# Revit family: W Shapes
name_source: partatom
category: Structural Framing
units: mm (PartAtom-declared; Revit-internal decimal feet)

## family parameters
Always export as geometry = No
Always vertical = Yes
Code Name = AISC 14.1
Cut with Voids When Loaded = No
Material for Model Behavior = Steel
OmniClass Number = 23.25.30.11.14.14
OmniClass Title = Beams
Section Shape = I-shape Parallel Flange
Shared = No
Show family pre-cut in plan views = Yes
Structural Framing Length Roundoff = 0' - 0"

## types (280) — shared parameters
Assembly Code = B10
Principal Axes Angle = 0.00°

## per-type parameters (varying)
| type | Bolt Spacing | Centroid Horizontal | Centroid Vertical | Elastic Modulus strong axis | Elastic Modulus weak axis | Flange Thickness | Height | Moment of Inertia strong axis | Moment of Inertia weak axis | Nominal Weight | Perimeter | Plastic Modulus strong axis | Plastic Modulus weak axis | Section Area | Section Name Key | Torsional Moment of Inertia | Warping Constant | Web Fillet | Web Thickness | Width |
| W12X26 | 0' - 3 1/2" | 3.245" | 6.100" | 33.40 in³ | 5.34 in³ | 0.380" | 12.200" | 204.0000 in⁴ | 17.3000 in⁴ | 26.00 lbf/ft | 49.40 ft²/ft | 37.20 in³ | 8.17 in³ | 7.65 in² | W12x26 | 0.3000 in⁴ | 607.00 in⁶ | 0.300" | 0.230" | 6.490" |
| W18X40 | 0' - 3 1/2" | 3.010" | 8.950" | 68.40 in³ | 6.35 in³ | 0.525" | 17.900" | 612.0000 in⁴ | 19.1000 in⁴ | 40.00 lbf/ft | 58.60 ft²/ft | 78.40 in³ | 10.00 in³ | 11.80 in² | W18x40 | 0.8100 in⁴ | 1440.00 in⁶ | 0.402" | 0.315" | 6.020" |
| W14x808 | 0' - 7 1/2" | 9.250" | 11.400" | 1400.00 in³ | 596.00 in³ | 5.120" | 22.800" | 16000.0000 in⁴ | 5550.0000 in⁴ | 808.00 lbf/ft | 111.34 ft²/ft | 1840.00 in³ | 930.00 in³ | 238.00 in² | W14x808 | 1840.0000 in⁴ | 435000.00 in⁶ | 0.600" | 3.740" | 18.500" |
| W14x873 | 0' - 7 1/2" | 9.350" | 11.800" | 1540.00 in³ | 655.00 in³ | 5.510" | 23.600" | 18200.0000 in⁴ | 6170.0000 in⁴ | 873.00 lbf/ft | 113.00 ft²/ft | 2030.00 in³ | 1020.00 in³ | 257.00 in² | W14x873 | 2270.0000 in⁴ | 505000.00 in⁶ | 0.600" | 3.940" | 18.700" |
| W36x723 | 0' - 7 1/2" | 8.900" | 20.900" | 2740.00 in³ | 415.00 in³ | 3.900" | 41.800" | 57200.0000 in⁴ | 3700.0000 in⁴ | 723.00 lbf/ft | 148.98 ft²/ft | 3270.00 in³ | 658.00 in³ | 213.00 in² | W36x723 | 785.0000 in⁴ | 1329000.00 in⁶ | 0.950" | 2.170" | 17.800" |
| W36x802 | 0' - 7 1/2" | 9.000" | 21.300" | 3040.00 in³ | 467.00 in³ | 4.290" | 42.600" | 64700.0000 in⁴ | 4210.0000 in⁴ | 802.00 lbf/ft | 151.06 ft²/ft | 3650.00 in³ | 744.00 in³ | 236.00 in² | W36x802 | 1040.0000 in⁴ | 1544000.00 in⁶ | 0.950" | 2.380" | 18.000" |
| W36x853 | 0' - 7 1/2" | 9.100" | 21.550" | 3240.00 in³ | 504.00 in³ | 4.530" | 43.100" | 69800.0000 in⁴ | 4600.0000 in⁴ | 853.00 lbf/ft | 152.36 ft²/ft | 3910.00 in³ | 805.00 in³ | 251.00 in² | W36x853 | 1240.0000 in⁴ | 1705000.00 in⁶ | 0.950" | 2.520" | 18.200" |
| W36x925 | 0' - 7 1/2" | 9.300" | 21.550" | 3380.00 in³ | 530.00 in³ | 4.530" | 43.100" | 72800.0000 in⁴ | 4940.0000 in⁴ | 925.00 lbf/ft | 153.27 ft²/ft | 4130.00 in³ | 862.00 in³ | 272.00 in² | W36x925 | 1430.0000 in⁴ | 1831000.00 in⁶ | 0.950" | 3.020" | 18.600" |
| W40x655 | 0' - 7 1/2" | 8.450" | 21.800" | 2600.00 in³ | 339.00 in³ | 3.540" | 43.600" | 56600.0000 in⁴ | 2870.0000 in⁴ | 655.00 lbf/ft | 148.66 ft²/ft | 3080.00 in³ | 542.00 in³ | 193.00 in² | W40x655 | 589.0000 in⁴ | 1154000.00 in⁶ | 0.790" | 1.970" | 16.900" |
| W4X13 | 0' - 2 1/4" | 2.030" | 2.080" | 5.46 in³ | 1.90 in³ | 0.345" | 4.160" | 11.3000 in⁴ | 3.8600 in⁴ | 13.00 lbf/ft | 23.60 ft²/ft | 6.28 in³ | 2.92 in³ | 3.83 in² | W4x13 | 0.1510 in⁴ | 14.00 in⁶ | 0.250" | 0.280" | 4.060" |
| W5X16 | 0' - 2 3/4" | 2.500" | 2.505" | 8.55 in³ | 3.00 in³ | 0.360" | 5.010" | 21.4000 in⁴ | 7.5100 in⁴ | 16.00 lbf/ft | 29.00 ft²/ft | 9.63 in³ | 4.58 in³ | 4.71 in² | W5x16 | 0.1920 in⁴ | 40.60 in⁶ | 0.300" | 0.240" | 5.000" |
| W5X19 | 0' - 2 3/4" | 2.515" | 2.575" | 10.20 in³ | 3.63 in³ | 0.430" | 5.150" | 26.3000 in⁴ | 9.1300 in⁴ | 19.00 lbf/ft | 29.40 ft²/ft | 11.60 in³ | 5.53 in³ | 5.56 in² | W5x19 | 0.3160 in⁴ | 50.90 in⁶ | 0.300" | 0.270" | 5.030" |
| W6X8.5 | 0' - 2 1/4" | 1.970" | 2.915" | 5.10 in³ | 1.01 in³ | 0.195" | 5.830" | 14.9000 in⁴ | 1.9900 in⁴ | 8.50 lbf/ft | 26.70 ft²/ft | 5.73 in³ | 1.56 in³ | 2.52 in² | W6x8.5 | 0.0333 in⁴ | 15.80 in⁶ | 0.250" | 0.170" | 3.940" |
| W6X9 | 0' - 2 1/4" | 1.970" | 2.950" | 5.56 in³ | 1.11 in³ | 0.215" | 5.900" | 16.4000 in⁴ | 2.2000 in⁴ | 9.00 lbf/ft | 26.80 ft²/ft | 6.23 in³ | 1.72 in³ | 2.68 in² | W6x9 | 0.0405 in⁴ | 17.70 in⁶ | 0.250" | 0.170" | 3.940" |
| W6X12 | 0' - 2 1/4" | 2.000" | 3.015" | 7.31 in³ | 1.50 in³ | 0.280" | 6.030" | 22.1000 in⁴ | 2.9900 in⁴ | 12.00 lbf/ft | 27.20 ft²/ft | 8.30 in³ | 2.32 in³ | 3.55 in² | W6x12 | 0.0903 in⁴ | 24.70 in⁶ | 0.250" | 0.230" | 4.000" |
| W6X15 | 0' - 3 1/2" | 2.995" | 2.995" | 9.72 in³ | 3.11 in³ | 0.260" | 5.990" | 29.1000 in⁴ | 9.3200 in⁴ | 15.00 lbf/ft | 35.10 ft²/ft | 10.80 in³ | 4.75 in³ | 4.43 in² | W6x15 | 0.1010 in⁴ | 76.50 in⁶ | 0.250" | 0.230" | 5.990" |
| W6X16 | 0' - 2 1/4" | 2.015" | 3.140" | 10.20 in³ | 2.20 in³ | 0.405" | 6.280" | 32.1000 in⁴ | 4.4300 in⁴ | 16.00 lbf/ft | 27.70 ft²/ft | 11.70 in³ | 3.39 in³ | 4.74 in² | W6x16 | 0.2230 in⁴ | 38.20 in⁶ | 0.250" | 0.260" | 4.030" |
| W6X20 | 0' - 3 1/2" | 3.010" | 3.100" | 13.40 in³ | 4.41 in³ | 0.365" | 6.200" | 41.4000 in⁴ | 13.3000 in⁴ | 20.00 lbf/ft | 35.50 ft²/ft | 15.00 in³ | 6.72 in³ | 5.87 in² | W6x20 | 0.2400 in⁴ | 113.00 in⁶ | 0.250" | 0.260" | 6.020" |
| W6X25 | 0' - 3 1/2" | 3.040" | 3.190" | 16.70 in³ | 5.61 in³ | 0.455" | 6.380" | 53.4000 in⁴ | 17.1000 in⁴ | 25.00 lbf/ft | 36.00 ft²/ft | 18.90 in³ | 8.56 in³ | 7.34 in² | W6x25 | 0.4610 in⁴ | 150.00 in⁶ | 0.250" | 0.320" | 6.080" |
| W8X10 | 0' - 2 1/4" | 1.970" | 3.945" | 7.81 in³ | 1.06 in³ | 0.205" | 7.890" | 30.8000 in⁴ | 2.0900 in⁴ | 10.00 lbf/ft | 30.70 ft²/ft | 8.87 in³ | 1.66 in³ | 2.96 in² | W8x10 | 0.0426 in⁴ | 30.90 in⁶ | 0.300" | 0.170" | 3.940" |
| W8X13 | 0' - 2 1/4" | 2.000" | 3.995" | 9.91 in³ | 1.37 in³ | 0.255" | 7.990" | 39.6000 in⁴ | 2.7300 in⁴ | 13.00 lbf/ft | 31.00 ft²/ft | 11.40 in³ | 2.15 in³ | 3.84 in² | W8x13 | 0.0871 in⁴ | 40.80 in⁶ | 0.300" | 0.230" | 4.000" |
| W8X15 | 0' - 2 1/4" | 2.008" | 4.055" | 11.80 in³ | 1.70 in³ | 0.315" | 8.110" | 48.0000 in⁴ | 3.4100 in⁴ | 15.00 lbf/ft | 31.30 ft²/ft | 13.60 in³ | 2.67 in³ | 4.44 in² | W8x15 | 0.1370 in⁴ | 51.80 in⁶ | 0.300" | 0.245" | 4.015" |
| W8X18 | 0' - 2 3/4" | 2.625" | 4.070" | 15.20 in³ | 3.04 in³ | 0.330" | 8.140" | 61.9000 in⁴ | 7.9700 in⁴ | 18.00 lbf/ft | 36.30 ft²/ft | 17.00 in³ | 4.66 in³ | 5.26 in² | W8x18 | 0.1720 in⁴ | 122.00 in⁶ | 0.300" | 0.230" | 5.250" |
| W8X21 | 0' - 2 3/4" | 2.635" | 4.140" | 18.20 in³ | 3.71 in³ | 0.400" | 8.280" | 75.3000 in⁴ | 9.7700 in⁴ | 21.00 lbf/ft | 36.60 ft²/ft | 20.40 in³ | 5.69 in³ | 6.16 in² | W8x21 | 0.2820 in⁴ | 152.00 in⁶ | 0.300" | 0.250" | 5.270" |
| W8X24 | 0' - 4" | 3.250" | 3.965" | 20.90 in³ | 5.63 in³ | 0.400" | 7.930" | 82.7000 in⁴ | 18.3000 in⁴ | 24.00 lbf/ft | 40.70 ft²/ft | 23.10 in³ | 8.57 in³ | 7.08 in² | W8x24 | 0.3460 in⁴ | 259.00 in⁶ | 0.394" | 0.245" | 6.500" |
| W8X28 | 0' - 4" | 3.270" | 4.030" | 24.30 in³ | 6.63 in³ | 0.465" | 8.060" | 98.0000 in⁴ | 21.7000 in⁴ | 28.00 lbf/ft | 41.00 ft²/ft | 27.20 in³ | 10.10 in³ | 8.25 in² | W8x28 | 0.5370 in⁴ | 312.00 in⁶ | 0.394" | 0.285" | 6.540" |
| W8X31 | 0' - 5 1/2" | 4.000" | 4.000" | 27.50 in³ | 9.27 in³ | 0.435" | 8.000" | 110.0000 in⁴ | 37.1000 in⁴ | 31.00 lbf/ft | 46.80 ft²/ft | 30.40 in³ | 14.10 in³ | 9.13 in² | W8x31 | 0.5360 in⁴ | 530.00 in⁶ | 0.394" | 0.285" | 8.000" |
| W8X35 | 0' - 5 1/2" | 4.010" | 4.060" | 31.20 in³ | 10.60 in³ | 0.495" | 8.120" | 127.0000 in⁴ | 42.6000 in⁴ | 35.00 lbf/ft | 47.00 ft²/ft | 34.70 in³ | 16.10 in³ | 10.30 in² | W8x35 | 0.7690 in⁴ | 619.00 in⁶ | 0.394" | 0.310" | 8.020" |
| W8X40 | 0' - 5 1/2" | 4.035" | 4.125" | 35.50 in³ | 12.20 in³ | 0.560" | 8.250" | 146.0000 in⁴ | 49.1000 in⁴ | 40.00 lbf/ft | 47.40 ft²/ft | 39.80 in³ | 18.50 in³ | 11.70 in² | W8x40 | 1.1200 in⁴ | 726.00 in⁶ | 0.394" | 0.360" | 8.070" |
| W8X48 | 0' - 5 1/2" | 4.055" | 4.250" | 43.20 in³ | 15.00 in³ | 0.685" | 8.500" | 184.0000 in⁴ | 60.9000 in⁴ | 48.00 lbf/ft | 48.00 ft²/ft | 49.00 in³ | 22.90 in³ | 14.10 in² | W8x48 | 1.9600 in⁴ | 931.00 in⁶ | 0.395" | 0.400" | 8.110" |
| W8X58 | 0' - 5 1/2" | 4.110" | 4.375" | 52.00 in³ | 18.30 in³ | 0.810" | 8.750" | 228.0000 in⁴ | 75.1000 in⁴ | 58.00 lbf/ft | 48.70 ft²/ft | 59.80 in³ | 27.90 in³ | 17.10 in² | W8x58 | 3.3300 in⁴ | 1180.00 in⁶ | 0.390" | 0.510" | 8.220" |
| W8X67 | 0' - 5 1/2" | 4.140" | 4.500" | 60.40 in³ | 21.40 in³ | 0.935" | 9.000" | 272.0000 in⁴ | 88.6000 in⁴ | 67.00 lbf/ft | 49.30 ft²/ft | 70.10 in³ | 32.70 in³ | 19.70 in² | W8x67 | 5.0500 in⁴ | 1440.00 in⁶ | 0.395" | 0.570" | 8.280" |
| W10X12 | 0' - 2 1/4" | 1.980" | 4.935" | 10.90 in³ | 1.10 in³ | 0.210" | 9.870" | 53.8000 in⁴ | 2.1800 in⁴ | 12.00 lbf/ft | 34.70 ft²/ft | 12.60 in³ | 1.74 in³ | 3.54 in² | W10x12 | 0.0547 in⁴ | 50.90 in⁶ | 0.300" | 0.190" | 3.960" |
| W10X15 | 0' - 2 1/4" | 2.000" | 4.995" | 13.80 in³ | 1.45 in³ | 0.270" | 9.990" | 68.9000 in⁴ | 2.8900 in⁴ | 15.00 lbf/ft | 35.00 ft²/ft | 16.00 in³ | 2.30 in³ | 4.41 in² | W10x15 | 0.1040 in⁴ | 68.30 in⁶ | 0.300" | 0.230" | 4.000" |
| W10X17 | 0' - 2 1/4" | 2.005" | 5.050" | 16.20 in³ | 1.78 in³ | 0.330" | 10.100" | 81.9000 in⁴ | 3.5600 in⁴ | 17.00 lbf/ft | 35.20 ft²/ft | 18.70 in³ | 2.80 in³ | 4.99 in² | W10x17 | 0.1560 in⁴ | 85.10 in⁶ | 0.300" | 0.240" | 4.010" |
| W10X19 | 0' - 2 1/4" | 2.010" | 5.100" | 18.80 in³ | 2.14 in³ | 0.395" | 10.200" | 96.3000 in⁴ | 4.2900 in⁴ | 19.00 lbf/ft | 35.50 ft²/ft | 21.60 in³ | 3.35 in³ | 5.62 in² | W10x19 | 0.2330 in⁴ | 104.00 in⁶ | 0.300" | 0.250" | 4.020" |
| W10X22 | 0' - 2 3/4" | 2.875" | 5.100" | 23.20 in³ | 3.97 in³ | 0.360" | 10.200" | 118.0000 in⁴ | 11.4000 in⁴ | 22.00 lbf/ft | 42.40 ft²/ft | 26.00 in³ | 6.10 in³ | 6.49 in² | W10x22 | 0.2390 in⁴ | 275.00 in⁶ | 0.300" | 0.240" | 5.750" |
| W10X26 | 0' - 2 3/4" | 2.885" | 5.150" | 27.90 in³ | 4.89 in³ | 0.440" | 10.300" | 144.0000 in⁴ | 14.1000 in⁴ | 26.00 lbf/ft | 42.60 ft²/ft | 31.30 in³ | 7.50 in³ | 7.61 in² | W10x26 | 0.4020 in⁴ | 345.00 in⁶ | 0.300" | 0.260" | 5.770" |
| W10X30 | 0' - 2 3/4" | 2.905" | 5.250" | 32.40 in³ | 5.75 in³ | 0.510" | 10.500" | 170.0000 in⁴ | 16.7000 in⁴ | 30.00 lbf/ft | 43.10 ft²/ft | 36.60 in³ | 8.84 in³ | 8.84 in² | W10x30 | 0.6220 in⁴ | 414.00 in⁶ | 0.300" | 0.300" | 5.810" |
| W10X33 | 0' - 5 1/2" | 3.980" | 4.865" | 35.00 in³ | 9.20 in³ | 0.435" | 9.730" | 171.0000 in⁴ | 36.6000 in⁴ | 33.00 lbf/ft | 49.90 ft²/ft | 38.80 in³ | 14.00 in³ | 9.71 in² | W10x33 | 0.5830 in⁴ | 791.00 in⁶ | 0.500" | 0.290" | 7.960" |
| W10X39 | 0' - 5 1/2" | 3.995" | 4.960" | 42.10 in³ | 11.30 in³ | 0.530" | 9.920" | 209.0000 in⁴ | 45.0000 in⁴ | 39.00 lbf/ft | 50.30 ft²/ft | 46.80 in³ | 17.20 in³ | 11.50 in² | W10x39 | 0.9760 in⁴ | 992.00 in⁶ | 0.500" | 0.315" | 7.990" |
| W10X45 | 0' - 5 1/2" | 4.010" | 5.050" | 49.10 in³ | 13.30 in³ | 0.620" | 10.100" | 248.0000 in⁴ | 53.4000 in⁴ | 45.00 lbf/ft | 50.70 ft²/ft | 54.90 in³ | 20.30 in³ | 13.30 in² | W10x45 | 1.5100 in⁴ | 1200.00 in⁶ | 0.500" | 0.350" | 8.020" |
| W10X49 | 0' - 5 1/2" | 5.000" | 5.000" | 54.60 in³ | 18.70 in³ | 0.560" | 10.000" | 272.0000 in⁴ | 93.4000 in⁴ | 49.00 lbf/ft | 58.50 ft²/ft | 60.40 in³ | 28.30 in³ | 14.40 in² | W10x49 | 1.3900 in⁴ | 2070.00 in⁶ | 0.500" | 0.340" | 10.000" |
| W10X54 | 0' - 5 1/2" | 5.000" | 5.050" | 60.00 in³ | 20.60 in³ | 0.615" | 10.100" | 303.0000 in⁴ | 103.0000 in⁴ | 54.00 lbf/ft | 58.60 ft²/ft | 66.60 in³ | 31.30 in³ | 15.80 in² | W10x54 | 1.8200 in⁴ | 2320.00 in⁶ | 0.505" | 0.370" | 10.000" |
| W10X60 | 0' - 5 1/2" | 5.050" | 5.100" | 66.70 in³ | 23.00 in³ | 0.680" | 10.200" | 341.0000 in⁴ | 116.0000 in⁴ | 60.00 lbf/ft | 59.10 ft²/ft | 74.60 in³ | 35.00 in³ | 17.70 in² | W10x60 | 2.4800 in⁴ | 2640.00 in⁶ | 0.500" | 0.420" | 10.100" |
| W10X68 | 0' - 5 1/2" | 5.050" | 5.200" | 75.70 in³ | 26.40 in³ | 0.770" | 10.400" | 394.0000 in⁴ | 134.0000 in⁴ | 68.00 lbf/ft | 59.40 ft²/ft | 85.30 in³ | 40.10 in³ | 19.90 in² | W10x68 | 3.5600 in⁴ | 3100.00 in⁶ | 0.500" | 0.470" | 10.100" |
| W10X77 | 0' - 5 1/2" | 5.100" | 5.300" | 85.90 in³ | 30.10 in³ | 0.870" | 10.600" | 455.0000 in⁴ | 154.0000 in⁴ | 77.00 lbf/ft | 60.10 ft²/ft | 97.60 in³ | 45.90 in³ | 22.70 in² | W10x77 | 5.1100 in⁴ | 3630.00 in⁶ | 0.500" | 0.530" | 10.200" |
| W10X88 | 0' - 5 1/2" | 5.150" | 5.400" | 98.50 in³ | 34.80 in³ | 0.990" | 10.800" | 534.0000 in⁴ | 179.0000 in⁴ | 88.00 lbf/ft | 60.70 ft²/ft | 113.00 in³ | 53.10 in³ | 26.00 in² | W10x88 | 7.5300 in⁴ | 4330.00 in⁶ | 0.500" | 0.605" | 10.300" |
| W10X100 | 0' - 5 1/2" | 5.150" | 5.550" | 112.00 in³ | 40.00 in³ | 1.120" | 11.100" | 623.0000 in⁴ | 207.0000 in⁴ | 100.00 lbf/ft | 61.20 ft²/ft | 130.00 in³ | 61.00 in³ | 29.30 in² | W10x100 | 10.9000 in⁴ | 5150.00 in⁶ | 0.500" | 0.680" | 10.300" |
| W10X112 | 0' - 5 1/2" | 5.200" | 5.700" | 126.00 in³ | 45.30 in³ | 1.250" | 11.400" | 716.0000 in⁴ | 236.0000 in⁴ | 112.00 lbf/ft | 62.00 ft²/ft | 147.00 in³ | 69.20 in³ | 32.90 in² | W10x112 | 15.1000 in⁴ | 6020.00 in⁶ | 0.500" | 0.755" | 10.400" |
| W12X14 | 0' - 2 1/4" | 1.985" | 5.950" | 14.90 in³ | 1.19 in³ | 0.225" | 11.900" | 88.6000 in⁴ | 2.3600 in⁴ | 14.00 lbf/ft | 38.80 ft²/ft | 17.40 in³ | 1.90 in³ | 4.16 in² | W12x14 | 0.0704 in⁴ | 80.40 in⁶ | 0.300" | 0.200" | 3.970" |
| W12X16 | 0' - 2 1/4" | 1.995" | 6.000" | 17.10 in³ | 1.41 in³ | 0.265" | 12.000" | 103.0000 in⁴ | 2.8200 in⁴ | 16.00 lbf/ft | 39.00 ft²/ft | 20.10 in³ | 2.26 in³ | 4.71 in² | W12x16 | 0.1030 in⁴ | 96.90 in⁶ | 0.300" | 0.220" | 3.990" |
| W12X19 | 0' - 2 1/4" | 2.005" | 6.100" | 21.30 in³ | 1.88 in³ | 0.350" | 12.200" | 130.0000 in⁴ | 3.7600 in⁴ | 19.00 lbf/ft | 39.50 ft²/ft | 24.70 in³ | 2.98 in³ | 5.57 in² | W12x19 | 0.1800 in⁴ | 131.00 in⁶ | 0.300" | 0.235" | 4.010" |
| W12X22 | 0' - 2 1/4" | 2.015" | 6.150" | 25.40 in³ | 2.31 in³ | 0.425" | 12.300" | 156.0000 in⁴ | 4.6600 in⁴ | 22.00 lbf/ft | 39.70 ft²/ft | 29.30 in³ | 3.66 in³ | 6.48 in² | W12x22 | 0.2930 in⁴ | 164.00 in⁶ | 0.300" | 0.260" | 4.030" |
| W12X30 | 0' - 3 1/2" | 3.260" | 6.150" | 38.60 in³ | 6.24 in³ | 0.440" | 12.300" | 238.0000 in⁴ | 20.3000 in⁴ | 30.00 lbf/ft | 49.60 ft²/ft | 43.10 in³ | 9.56 in³ | 8.79 in² | W12x30 | 0.4570 in⁴ | 720.00 in⁶ | 0.300" | 0.260" | 6.520" |
| W12X35 | 0' - 3 1/2" | 3.280" | 6.250" | 45.60 in³ | 7.47 in³ | 0.520" | 12.500" | 285.0000 in⁴ | 24.5000 in⁴ | 35.00 lbf/ft | 50.10 ft²/ft | 51.20 in³ | 11.50 in³ | 10.30 in² | W12x35 | 0.7410 in⁴ | 879.00 in⁶ | 0.300" | 0.300" | 6.560" |
| W12X40 | 0' - 5 1/2" | 4.005" | 5.950" | 51.50 in³ | 11.00 in³ | 0.515" | 11.900" | 307.0000 in⁴ | 44.1000 in⁴ | 40.00 lbf/ft | 54.40 ft²/ft | 57.00 in³ | 16.80 in³ | 11.70 in² | W12x40 | 0.9060 in⁴ | 1440.00 in⁶ | 0.505" | 0.295" | 8.010" |
| W12X45 | 0' - 5 1/2" | 4.025" | 6.050" | 57.70 in³ | 12.40 in³ | 0.575" | 12.100" | 348.0000 in⁴ | 50.0000 in⁴ | 45.00 lbf/ft | 54.90 ft²/ft | 64.20 in³ | 19.00 in³ | 13.10 in² | W12x45 | 1.2600 in⁴ | 1650.00 in⁶ | 0.505" | 0.335" | 8.050" |
| W12X50 | 0' - 5 1/2" | 4.040" | 6.100" | 64.20 in³ | 13.90 in³ | 0.640" | 12.200" | 391.0000 in⁴ | 56.3000 in⁴ | 50.00 lbf/ft | 55.10 ft²/ft | 71.90 in³ | 21.30 in³ | 14.60 in² | W12x50 | 1.7100 in⁴ | 1880.00 in⁶ | 0.500" | 0.370" | 8.080" |
| W12X53 | 0' - 5 1/2" | 5.000" | 6.050" | 70.60 in³ | 19.20 in³ | 0.575" | 12.100" | 425.0000 in⁴ | 95.8000 in⁴ | 53.00 lbf/ft | 62.50 ft²/ft | 77.90 in³ | 29.10 in³ | 15.60 in² | W12x53 | 1.5800 in⁴ | 3160.00 in⁶ | 0.605" | 0.345" | 10.000" |
| W12X58 | 0' - 5 1/2" | 5.000" | 6.100" | 78.00 in³ | 21.40 in³ | 0.640" | 12.200" | 475.0000 in⁴ | 107.0000 in⁴ | 58.00 lbf/ft | 62.60 ft²/ft | 86.40 in³ | 32.50 in³ | 17.00 in² | W12x58 | 2.1000 in⁴ | 3570.00 in⁶ | 0.600" | 0.360" | 10.000" |
| W12X65 | 0' - 5 1/2" | 6.000" | 6.050" | 87.90 in³ | 29.10 in³ | 0.605" | 12.100" | 533.0000 in⁴ | 174.0000 in⁴ | 65.00 lbf/ft | 70.40 ft²/ft | 96.80 in³ | 44.10 in³ | 19.10 in² | W12x65 | 2.1800 in⁴ | 5780.00 in⁶ | 0.595" | 0.390" | 12.000" |
| W12X72 | 0' - 5 1/2" | 6.000" | 6.150" | 97.40 in³ | 32.40 in³ | 0.670" | 12.300" | 597.0000 in⁴ | 195.0000 in⁴ | 72.00 lbf/ft | 70.70 ft²/ft | 108.00 in³ | 49.20 in³ | 21.10 in² | W12x72 | 2.9300 in⁴ | 6540.00 in⁶ | 0.600" | 0.430" | 12.000" |
| W12X79 | 0' - 5 1/2" | 6.050" | 6.200" | 107.00 in³ | 35.80 in³ | 0.735" | 12.400" | 662.0000 in⁴ | 216.0000 in⁴ | 79.00 lbf/ft | 71.20 ft²/ft | 119.00 in³ | 54.30 in³ | 23.20 in² | W12x79 | 3.8400 in⁴ | 7330.00 in⁶ | 0.595" | 0.470" | 12.100" |
| W12X87 | 0' - 5 1/2" | 6.050" | 6.250" | 118.00 in³ | 39.70 in³ | 0.810" | 12.500" | 740.0000 in⁴ | 241.0000 in⁴ | 87.00 lbf/ft | 71.30 ft²/ft | 132.00 in³ | 60.40 in³ | 25.60 in² | W12x87 | 5.1000 in⁴ | 8270.00 in⁶ | 0.600" | 0.515" | 12.100" |
| W12X96 | 0' - 5 1/2" | 6.100" | 6.350" | 131.00 in³ | 44.40 in³ | 0.900" | 12.700" | 833.0000 in⁴ | 270.0000 in⁴ | 96.00 lbf/ft | 72.10 ft²/ft | 147.00 in³ | 67.50 in³ | 28.20 in² | W12x96 | 6.8500 in⁴ | 9410.00 in⁶ | 0.600" | 0.550" | 12.200" |
| W12X106 | 0' - 5 1/2" | 6.100" | 6.450" | 145.00 in³ | 49.30 in³ | 0.990" | 12.900" | 933.0000 in⁴ | 301.0000 in⁴ | 106.00 lbf/ft | 72.40 ft²/ft | 164.00 in³ | 75.10 in³ | 31.20 in² | W12x106 | 9.1300 in⁴ | 10700.00 in⁶ | 0.600" | 0.610" | 12.200" |
| W12X120 | 0' - 5 1/2" | 6.150" | 6.550" | 163.00 in³ | 56.00 in³ | 1.110" | 13.100" | 1070.0000 in⁴ | 345.0000 in⁴ | 120.00 lbf/ft | 73.00 ft²/ft | 186.00 in³ | 85.40 in³ | 35.20 in² | W12x120 | 12.9000 in⁴ | 12400.00 in⁶ | 0.590" | 0.710" | 12.300" |
| W12X136 | 0' - 5 1/2" | 6.200" | 6.700" | 186.00 in³ | 64.20 in³ | 1.250" | 13.400" | 1240.0000 in⁴ | 398.0000 in⁴ | 136.00 lbf/ft | 73.80 ft²/ft | 214.00 in³ | 98.00 in³ | 39.90 in² | W12x136 | 18.5000 in⁴ | 14700.00 in⁶ | 0.600" | 0.790" | 12.400" |
| W12X152 | 0' - 5 1/2" | 6.250" | 6.850" | 209.00 in³ | 72.80 in³ | 1.400" | 13.700" | 1430.0000 in⁴ | 454.0000 in⁴ | 152.00 lbf/ft | 74.60 ft²/ft | 243.00 in³ | 111.00 in³ | 44.70 in² | W12x152 | 25.8000 in⁴ | 17200.00 in⁶ | 0.600" | 0.870" | 12.500" |
| W12X170 | 0' - 5 1/2" | 6.300" | 7.000" | 235.00 in³ | 82.30 in³ | 1.560" | 14.000" | 1650.0000 in⁴ | 517.0000 in⁴ | 170.00 lbf/ft | 75.50 ft²/ft | 275.00 in³ | 126.00 in³ | 50.00 in² | W12x170 | 35.6000 in⁴ | 20100.00 in⁶ | 0.600" | 0.960" | 12.600" |
| W12X190 | 0' - 5 1/2" | 6.350" | 7.200" | 263.00 in³ | 93.00 in³ | 1.740" | 14.400" | 1890.0000 in⁴ | 589.0000 in⁴ | 190.00 lbf/ft | 76.50 ft²/ft | 311.00 in³ | 143.00 in³ | 56.00 in² | W12x190 | 48.8000 in⁴ | 23600.00 in⁶ | 0.590" | 1.060" | 12.700" |
| W12X210 | 0' - 5 1/2" | 6.400" | 7.350" | 292.00 in³ | 104.00 in³ | 1.900" | 14.700" | 2140.0000 in⁴ | 664.0000 in⁴ | 210.00 lbf/ft | 77.20 ft²/ft | 348.00 in³ | 159.00 in³ | 61.80 in² | W12x210 | 64.7000 in⁴ | 27200.00 in⁶ | 0.600" | 1.180" | 12.800" |
| W12X230 | 0' - 5 1/2" | 6.450" | 7.550" | 321.00 in³ | 115.00 in³ | 2.070" | 15.100" | 2420.0000 in⁴ | 742.0000 in⁴ | 230.00 lbf/ft | 78.20 ft²/ft | 386.00 in³ | 177.00 in³ | 67.70 in² | W12x230 | 83.8000 in⁴ | 31200.00 in⁶ | 0.600" | 1.290" | 12.900" |
| W12X252 | 0' - 5 1/2" | 6.500" | 7.700" | 353.00 in³ | 127.00 in³ | 2.250" | 15.400" | 2720.0000 in⁴ | 828.0000 in⁴ | 252.00 lbf/ft | 79.00 ft²/ft | 428.00 in³ | 196.00 in³ | 74.10 in² | W12x252 | 108.0000 in⁴ | 35800.00 in⁶ | 0.600" | 1.400" | 13.000" |
| W12X279 | 0' - 5 1/2" | 6.550" | 7.950" | 393.00 in³ | 143.00 in³ | 2.470" | 15.900" | 3110.0000 in⁴ | 937.0000 in⁴ | 279.00 lbf/ft | 80.10 ft²/ft | 481.00 in³ | 220.00 in³ | 81.90 in² | W12x279 | 143.0000 in⁴ | 42000.00 in⁶ | 0.600" | 1.530" | 13.100" |
| W12X305 | 0' - 5 1/2" | 6.600" | 8.150" | 435.00 in³ | 159.00 in³ | 2.710" | 16.300" | 3550.0000 in⁴ | 1050.0000 in⁴ | 305.00 lbf/ft | 81.10 ft²/ft | 537.00 in³ | 244.00 in³ | 89.50 in² | W12x305 | 185.0000 in⁴ | 48600.00 in⁶ | 0.590" | 1.630" | 13.200" |
| W12X336 | 0' - 5 1/2" | 6.700" | 8.400" | 483.00 in³ | 177.00 in³ | 2.960" | 16.800" | 4060.0000 in⁴ | 1190.0000 in⁴ | 336.00 lbf/ft | 82.60 ft²/ft | 603.00 in³ | 274.00 in³ | 98.90 in² | W12x336 | 243.0000 in⁴ | 57000.00 in⁶ | 0.590" | 1.780" | 13.400" |
| W14X22 | 0' - 2 3/4" | 2.500" | 6.850" | 29.00 in³ | 2.80 in³ | 0.335" | 13.700" | 199.0000 in⁴ | 7.0000 in⁴ | 22.00 lbf/ft | 46.70 ft²/ft | 33.20 in³ | 4.39 in³ | 6.49 in² | W14x22 | 0.2080 in⁴ | 314.00 in⁶ | 0.400" | 0.230" | 5.000" |
| W14X26 | 0' - 3 1/2" | 2.515" | 6.950" | 35.30 in³ | 3.55 in³ | 0.420" | 13.900" | 245.0000 in⁴ | 8.9100 in⁴ | 26.00 lbf/ft | 53.30 ft²/ft | 40.20 in³ | 5.54 in³ | 7.69 in² | W14x26 | 0.3580 in⁴ | 405.00 in⁶ | 0.400" | 0.255" | 5.030" |
| W14X30 | 0' - 3 1/2" | 3.365" | 6.900" | 42.00 in³ | 5.82 in³ | 0.385" | 13.800" | 291.0000 in⁴ | 19.6000 in⁴ | 30.00 lbf/ft | 53.70 ft²/ft | 47.30 in³ | 8.99 in³ | 8.85 in² | W14x30 | 0.3800 in⁴ | 887.00 in⁶ | 0.400" | 0.270" | 6.730" |
| W14X34 | 0' - 7 1/2" | 3.375" | 7.000" | 48.60 in³ | 6.91 in³ | 0.455" | 14.000" | 340.0000 in⁴ | 23.3000 in⁴ | 34.00 lbf/ft | 97.50 ft²/ft | 54.60 in³ | 10.60 in³ | 10.00 in² | W14x34 | 0.5690 in⁴ | 1070.00 in⁶ | 0.400" | 0.285" | 6.750" |
| W14X38 | 0' - 3 1/2" | 3.385" | 7.050" | 54.60 in³ | 7.88 in³ | 0.515" | 14.100" | 385.0000 in⁴ | 26.7000 in⁴ | 38.00 lbf/ft | 54.00 ft²/ft | 61.50 in³ | 12.10 in³ | 11.20 in² | W14x38 | 0.7980 in⁴ | 1230.00 in⁶ | 0.400" | 0.310" | 6.770" |
| W14X43 | 0' - 5 1/2" | 4.000" | 6.850" | 62.60 in³ | 11.30 in³ | 0.530" | 13.700" | 428.0000 in⁴ | 45.2000 in⁴ | 43.00 lbf/ft | 57.80 ft²/ft | 69.60 in³ | 17.30 in³ | 12.60 in² | W14x43 | 1.0500 in⁴ | 1950.00 in⁶ | 0.590" | 0.305" | 8.000" |
| W14X48 | 0' - 5 1/2" | 4.015" | 6.900" | 70.20 in³ | 12.80 in³ | 0.595" | 13.800" | 484.0000 in⁴ | 51.4000 in⁴ | 48.00 lbf/ft | 58.00 ft²/ft | 78.40 in³ | 19.60 in³ | 14.10 in² | W14x48 | 1.4500 in⁴ | 2240.00 in⁶ | 0.595" | 0.340" | 8.030" |
| W14X53 | 0' - 5 1/2" | 4.030" | 6.950" | 77.80 in³ | 14.30 in³ | 0.660" | 13.900" | 541.0000 in⁴ | 57.7000 in⁴ | 53.00 lbf/ft | 58.30 ft²/ft | 87.10 in³ | 22.00 in³ | 15.60 in² | W14x53 | 1.9400 in⁴ | 2540.00 in⁶ | 0.590" | 0.370" | 8.060" |
| W14X61 | 0' - 5 1/2" | 5.000" | 6.950" | 92.10 in³ | 21.50 in³ | 0.645" | 13.900" | 640.0000 in⁴ | 107.0000 in⁴ | 61.00 lbf/ft | 66.00 ft²/ft | 102.00 in³ | 32.80 in³ | 17.90 in² | W14x61 | 2.1900 in⁴ | 4710.00 in⁶ | 0.595" | 0.375" | 10.000" |
| W14X68 | 0' - 5 1/2" | 5.000" | 7.000" | 103.00 in³ | 24.20 in³ | 0.720" | 14.000" | 722.0000 in⁴ | 121.0000 in⁴ | 68.00 lbf/ft | 66.20 ft²/ft | 115.00 in³ | 36.90 in³ | 20.00 in² | W14x68 | 3.0100 in⁴ | 5380.00 in⁶ | 0.590" | 0.415" | 10.000" |
| W14X74 | 0' - 5 1/2" | 5.050" | 7.100" | 112.00 in³ | 26.60 in³ | 0.785" | 14.200" | 795.0000 in⁴ | 134.0000 in⁴ | 74.00 lbf/ft | 66.90 ft²/ft | 126.00 in³ | 40.50 in³ | 21.80 in² | W14x74 | 3.8700 in⁴ | 5990.00 in⁶ | 0.595" | 0.450" | 10.100" |
| W14X82 | 0' - 5 1/2" | 5.050" | 7.150" | 123.00 in³ | 29.30 in³ | 0.855" | 14.300" | 881.0000 in⁴ | 148.0000 in⁴ | 82.00 lbf/ft | 67.00 ft²/ft | 139.00 in³ | 44.80 in³ | 24.00 in² | W14x82 | 5.0700 in⁴ | 6710.00 in⁶ | 0.595" | 0.510" | 10.100" |
| W14X90 | 0' - 5 1/2" | 7.250" | 7.000" | 143.00 in³ | 49.90 in³ | 0.710" | 14.000" | 999.0000 in⁴ | 362.0000 in⁴ | 90.00 lbf/ft | 84.10 ft²/ft | 157.00 in³ | 75.60 in³ | 26.50 in² | W14x90 | 4.0600 in⁴ | 16000.00 in⁶ | 0.600" | 0.440" | 14.500" |
| W14X99 | 0' - 5 1/2" | 7.300" | 7.100" | 157.00 in³ | 55.20 in³ | 0.780" | 14.200" | 1110.0000 in⁴ | 402.0000 in⁴ | 99.00 lbf/ft | 84.80 ft²/ft | 173.00 in³ | 83.60 in³ | 29.10 in² | W14x99 | 5.3700 in⁴ | 18000.00 in⁶ | 0.600" | 0.485" | 14.600" |
| W14X109 | 0' - 2 3/4" | 7.300" | 7.150" | 173.00 in³ | 61.20 in³ | 0.860" | 14.300" | 1240.0000 in⁴ | 447.0000 in⁴ | 109.00 lbf/ft | 46.30 ft²/ft | 192.00 in³ | 92.70 in³ | 32.00 in² | W14x109 | 7.1200 in⁴ | 20200.00 in⁶ | 0.600" | 0.525" | 14.600" |
| W14X120 | 0' - 5 1/2" | 7.350" | 7.250" | 190.00 in³ | 67.50 in³ | 0.940" | 14.500" | 1380.0000 in⁴ | 495.0000 in⁴ | 120.00 lbf/ft | 84.90 ft²/ft | 212.00 in³ | 102.00 in³ | 35.30 in² | W14x120 | 9.3700 in⁴ | 22700.00 in⁶ | 0.600" | 0.590" | 14.700" |
| W14X132 | 0' - 5 1/2" | 7.350" | 7.350" | 209.00 in³ | 74.50 in³ | 1.030" | 14.700" | 1530.0000 in⁴ | 548.0000 in⁴ | 132.00 lbf/ft | 85.60 ft²/ft | 234.00 in³ | 113.00 in³ | 38.80 in² | W14x132 | 12.3000 in⁴ | 25500.00 in⁶ | 0.600" | 0.645" | 14.700" |
| W14X145 | 0' - 5 1/2" | 7.750" | 7.400" | 232.00 in³ | 87.30 in³ | 1.090" | 14.800" | 1710.0000 in⁴ | 677.0000 in⁴ | 145.00 lbf/ft | 85.90 ft²/ft | 260.00 in³ | 133.00 in³ | 42.70 in² | W14x145 | 15.2000 in⁴ | 31700.00 in⁶ | 0.600" | 0.680" | 15.500" |
| W14X159 | 0' - 7 1/2" | 7.800" | 7.500" | 254.00 in³ | 96.20 in³ | 1.190" | 15.000" | 1900.0000 in⁴ | 748.0000 in⁴ | 159.00 lbf/ft | 89.20 ft²/ft | 287.00 in³ | 146.00 in³ | 46.70 in² | W14x159 | 19.7000 in⁴ | 35600.00 in⁶ | 0.600" | 0.745" | 15.600" |
| W14X176 | 0' - 7 1/2" | 7.850" | 7.600" | 281.00 in³ | 107.00 in³ | 1.310" | 15.200" | 2140.0000 in⁴ | 838.0000 in⁴ | 176.00 lbf/ft | 89.90 ft²/ft | 320.00 in³ | 163.00 in³ | 51.80 in² | W14x176 | 26.5000 in⁴ | 40500.00 in⁶ | 0.600" | 0.830" | 15.700" |
| W14X193 | 0' - 7 1/2" | 7.850" | 7.750" | 310.00 in³ | 119.00 in³ | 1.440" | 15.500" | 2400.0000 in⁴ | 931.0000 in⁴ | 193.00 lbf/ft | 90.50 ft²/ft | 355.00 in³ | 180.00 in³ | 56.80 in² | W14x193 | 34.8000 in⁴ | 45900.00 in⁶ | 0.600" | 0.890" | 15.700" |
| W14X211 | 0' - 7 1/2" | 7.900" | 7.850" | 338.00 in³ | 130.00 in³ | 1.560" | 15.700" | 2660.0000 in⁴ | 1030.0000 in⁴ | 211.00 lbf/ft | 91.00 ft²/ft | 390.00 in³ | 198.00 in³ | 62.00 in² | W14x211 | 44.6000 in⁴ | 51500.00 in⁶ | 0.600" | 0.980" | 15.800" |
| W14X233 | 0' - 7 1/2" | 7.950" | 8.000" | 375.00 in³ | 145.00 in³ | 1.720" | 16.000" | 3010.0000 in⁴ | 1150.0000 in⁴ | 233.00 lbf/ft | 91.60 ft²/ft | 436.00 in³ | 221.00 in³ | 68.50 in² | W14x233 | 59.5000 in⁴ | 59000.00 in⁶ | 0.600" | 1.070" | 15.900" |
| W14X257 | 0' - 7 1/2" | 8.000" | 8.200" | 415.00 in³ | 161.00 in³ | 1.890" | 16.400" | 3400.0000 in⁴ | 1290.0000 in⁴ | 257.00 lbf/ft | 92.40 ft²/ft | 487.00 in³ | 246.00 in³ | 75.60 in² | W14x257 | 79.1000 in⁴ | 67800.00 in⁶ | 0.600" | 1.180" | 16.000" |
| W14X283 | 0' - 7 1/2" | 8.050" | 8.350" | 459.00 in³ | 179.00 in³ | 2.070" | 16.700" | 3840.0000 in⁴ | 1440.0000 in⁴ | 283.00 lbf/ft | 93.40 ft²/ft | 542.00 in³ | 274.00 in³ | 83.30 in² | W14x283 | 104.0000 in⁴ | 77700.00 in⁶ | 0.600" | 1.290" | 16.100" |
| W14X311 | 0' - 7 1/2" | 8.100" | 8.550" | 506.00 in³ | 199.00 in³ | 2.260" | 17.100" | 4330.0000 in⁴ | 1610.0000 in⁴ | 311.00 lbf/ft | 94.20 ft²/ft | 603.00 in³ | 304.00 in³ | 91.40 in² | W14x311 | 136.0000 in⁴ | 89100.00 in⁶ | 0.600" | 1.410" | 16.200" |
| W14X342 | 0' - 7 1/2" | 8.200" | 8.750" | 558.00 in³ | 221.00 in³ | 2.470" | 17.500" | 4900.0000 in⁴ | 1810.0000 in⁴ | 342.00 lbf/ft | 95.20 ft²/ft | 672.00 in³ | 338.00 in³ | 101.00 in² | W14x342 | 178.0000 in⁴ | 103000.00 in⁶ | 0.600" | 1.540" | 16.400" |
| W14X370 | 0' - 7 1/2" | 8.250" | 8.950" | 607.00 in³ | 241.00 in³ | 2.660" | 17.900" | 5440.0000 in⁴ | 1990.0000 in⁴ | 370.00 lbf/ft | 96.50 ft²/ft | 736.00 in³ | 370.00 in³ | 109.00 in² | W14x370 | 222.0000 in⁴ | 116000.00 in⁶ | 0.600" | 1.660" | 16.500" |
| W14X398 | 0' - 7 1/2" | 8.300" | 9.150" | 656.00 in³ | 262.00 in³ | 2.850" | 18.300" | 6000.0000 in⁴ | 2170.0000 in⁴ | 398.00 lbf/ft | 98.40 ft²/ft | 801.00 in³ | 402.00 in³ | 117.00 in² | W14x398 | 273.0000 in⁴ | 129000.00 in⁶ | 0.590" | 1.770" | 16.600" |
| W14X426 | 0' - 7 1/2" | 8.350" | 9.350" | 706.00 in³ | 283.00 in³ | 3.040" | 18.700" | 6600.0000 in⁴ | 2360.0000 in⁴ | 426.00 lbf/ft | 99.40 ft²/ft | 869.00 in³ | 434.00 in³ | 125.00 in² | W14x426 | 331.0000 in⁴ | 144000.00 in⁶ | 0.590" | 1.880" | 16.700" |
| W14X455 | 0' - 7 1/2" | 8.400" | 9.500" | 756.00 in³ | 304.00 in³ | 3.210" | 19.000" | 7190.0000 in⁴ | 2560.0000 in⁴ | 455.00 lbf/ft | 100.00 ft²/ft | 936.00 in³ | 468.00 in³ | 134.00 in² | W14x455 | 395.0000 in⁴ | 160000.00 in⁶ | 0.600" | 2.020" | 16.800" |
| W14X500 | 0' - 7 1/2" | 8.500" | 9.800" | 838.00 in³ | 339.00 in³ | 3.500" | 19.600" | 8210.0000 in⁴ | 2880.0000 in⁴ | 500.00 lbf/ft | 102.00 ft²/ft | 1050.00 in³ | 522.00 in³ | 147.00 in² | W14x500 | 514.0000 in⁴ | 187000.00 in⁶ | 0.600" | 2.190" | 17.000" |
| W14X550 | 0' - 7 1/2" | 8.600" | 10.100" | 931.00 in³ | 378.00 in³ | 3.820" | 20.200" | 9430.0000 in⁴ | 3250.0000 in⁴ | 550.00 lbf/ft | 103.00 ft²/ft | 1180.00 in³ | 583.00 in³ | 162.00 in² | W14x550 | 669.0000 in⁴ | 219000.00 in⁶ | 0.600" | 2.380" | 17.200" |
| W14X605 | 0' - 7 1/2" | 8.700" | 10.450" | 1040.00 in³ | 423.00 in³ | 4.160" | 20.900" | 10800.0000 in⁴ | 3680.0000 in⁴ | 605.00 lbf/ft | 105.00 ft²/ft | 1320.00 in³ | 652.00 in³ | 178.00 in² | W14x605 | 869.0000 in⁴ | 258000.00 in⁶ | 0.600" | 2.600" | 17.400" |
| W14X665 | 0' - 7 1/2" | 8.850" | 10.800" | 1150.00 in³ | 472.00 in³ | 4.520" | 21.600" | 12400.0000 in⁴ | 4170.0000 in⁴ | 665.00 lbf/ft | 107.00 ft²/ft | 1480.00 in³ | 730.00 in³ | 196.00 in² | W14x665 | 1120.0000 in⁴ | 305000.00 in⁶ | 0.600" | 2.830" | 17.700" |
| W14X730 | 0' - 7 1/2" | 8.950" | 11.200" | 1280.00 in³ | 527.00 in³ | 4.910" | 22.400" | 14300.0000 in⁴ | 4720.0000 in⁴ | 730.00 lbf/ft | 109.00 ft²/ft | 1660.00 in³ | 816.00 in³ | 215.00 in² | W14x730 | 1450.0000 in⁴ | 362000.00 in⁶ | 0.600" | 3.070" | 17.900" |
| W16X26 | 0' - 3 1/2" | 2.750" | 7.850" | 38.40 in³ | 3.49 in³ | 0.345" | 15.700" | 301.0000 in⁴ | 9.5900 in⁴ | 26.00 lbf/ft | 52.20 ft²/ft | 44.20 in³ | 5.48 in³ | 7.68 in² | W16x26 | 0.2620 in⁴ | 565.00 in⁶ | 0.402" | 0.250" | 5.500" |
| W16X31 | 0' - 3 1/2" | 2.765" | 7.950" | 47.20 in³ | 4.49 in³ | 0.440" | 15.900" | 375.0000 in⁴ | 12.4000 in⁴ | 31.00 lbf/ft | 52.70 ft²/ft | 54.00 in³ | 7.03 in³ | 9.13 in² | W16x31 | 0.4610 in⁴ | 739.00 in⁶ | 0.402" | 0.275" | 5.530" |
| W16X36 | 0' - 3 1/2" | 3.495" | 7.950" | 56.50 in³ | 7.00 in³ | 0.430" | 15.900" | 448.0000 in⁴ | 24.5000 in⁴ | 36.00 lbf/ft | 58.50 ft²/ft | 64.00 in³ | 10.80 in³ | 10.60 in² | W16x36 | 0.5450 in⁴ | 1460.00 in⁶ | 0.402" | 0.295" | 6.990" |
| W16X40 | 0' - 3 1/2" | 3.500" | 8.000" | 64.70 in³ | 8.25 in³ | 0.505" | 16.000" | 518.0000 in⁴ | 28.9000 in⁴ | 40.00 lbf/ft | 58.70 ft²/ft | 73.00 in³ | 12.70 in³ | 11.80 in² | W16x40 | 0.7940 in⁴ | 1730.00 in⁶ | 0.402" | 0.305" | 7.000" |
| W16X45 | 0' - 3 1/2" | 3.520" | 8.050" | 72.70 in³ | 9.34 in³ | 0.565" | 16.100" | 586.0000 in⁴ | 32.8000 in⁴ | 45.00 lbf/ft | 59.00 ft²/ft | 82.30 in³ | 14.50 in³ | 13.30 in² | W16x45 | 1.1100 in⁴ | 1990.00 in⁶ | 0.402" | 0.345" | 7.040" |
| W16X50 | 0' - 3 1/2" | 3.535" | 8.150" | 81.00 in³ | 10.50 in³ | 0.630" | 16.300" | 659.0000 in⁴ | 37.2000 in⁴ | 50.00 lbf/ft | 59.40 ft²/ft | 92.00 in³ | 16.30 in³ | 14.70 in² | W16x50 | 1.5200 in⁴ | 2270.00 in⁶ | 0.400" | 0.380" | 7.070" |
| W16X57 | 0' - 3 1/2" | 3.560" | 8.200" | 92.20 in³ | 12.10 in³ | 0.715" | 16.400" | 758.0000 in⁴ | 43.1000 in⁴ | 57.00 lbf/ft | 59.70 ft²/ft | 105.00 in³ | 18.90 in³ | 16.80 in² | W16x57 | 2.2200 in⁴ | 2660.00 in⁶ | 0.405" | 0.430" | 7.120" |
| W16X67 | 0' - 5 1/2" | 5.100" | 8.150" | 117.00 in³ | 23.20 in³ | 0.665" | 16.300" | 954.0000 in⁴ | 119.0000 in⁴ | 67.00 lbf/ft | 71.90 ft²/ft | 130.00 in³ | 35.50 in³ | 19.60 in² | W16x67 | 2.3900 in⁴ | 7300.00 in⁶ | 0.405" | 0.395" | 10.200" |
| W16X77 | 0' - 5 1/2" | 5.150" | 8.250" | 134.00 in³ | 26.90 in³ | 0.760" | 16.500" | 1110.0000 in⁴ | 138.0000 in⁴ | 77.00 lbf/ft | 72.60 ft²/ft | 150.00 in³ | 41.10 in³ | 22.60 in² | W16x77 | 3.5700 in⁴ | 8590.00 in⁶ | 0.400" | 0.455" | 10.300" |
| W16X89 | 0' - 5 1/2" | 5.200" | 8.400" | 155.00 in³ | 31.40 in³ | 0.875" | 16.800" | 1300.0000 in⁴ | 163.0000 in⁴ | 89.00 lbf/ft | 73.50 ft²/ft | 175.00 in³ | 48.10 in³ | 26.20 in² | W16x89 | 5.4500 in⁴ | 10200.00 in⁶ | 0.405" | 0.525" | 10.400" |
| W16X100 | 0' - 5 1/2" | 5.200" | 8.500" | 175.00 in³ | 35.70 in³ | 0.985" | 17.000" | 1490.0000 in⁴ | 186.0000 in⁴ | 100.00 lbf/ft | 73.70 ft²/ft | 198.00 in³ | 54.90 in³ | 29.40 in² | W16x100 | 7.7300 in⁴ | 11900.00 in⁶ | 0.405" | 0.585" | 10.400" |
| W18X35 | 0' - 3 1/2" | 3.000" | 8.850" | 57.60 in³ | 5.12 in³ | 0.425" | 17.700" | 510.0000 in⁴ | 15.3000 in⁴ | 35.00 lbf/ft | 58.10 ft²/ft | 66.50 in³ | 8.06 in³ | 10.30 in² | W18x35 | 0.5060 in⁴ | 1140.00 in⁶ | 0.402" | 0.300" | 6.000" |
| W18X46 | 0' - 3 1/2" | 3.030" | 9.050" | 78.80 in³ | 7.43 in³ | 0.605" | 18.100" | 712.0000 in⁴ | 22.5000 in⁴ | 46.00 lbf/ft | 59.00 ft²/ft | 90.70 in³ | 11.70 in³ | 13.50 in² | W18x46 | 1.2200 in⁴ | 1720.00 in⁶ | 0.405" | 0.360" | 6.060" |
| W18X50 | 0' - 3 1/2" | 3.750" | 9.000" | 88.90 in³ | 10.70 in³ | 0.570" | 18.000" | 800.0000 in⁴ | 40.1000 in⁴ | 50.00 lbf/ft | 64.60 ft²/ft | 101.00 in³ | 16.60 in³ | 14.70 in² | W18x50 | 1.2400 in⁴ | 3040.00 in⁶ | 0.402" | 0.355" | 7.500" |
| W18X55 | 0' - 3 1/2" | 3.765" | 9.050" | 98.30 in³ | 11.90 in³ | 0.630" | 18.100" | 890.0000 in⁴ | 44.9000 in⁴ | 55.00 lbf/ft | 64.80 ft²/ft | 112.00 in³ | 18.50 in³ | 16.20 in² | W18x55 | 1.6600 in⁴ | 3430.00 in⁶ | 0.400" | 0.390" | 7.530" |
| W18X60 | 0' - 3 1/2" | 3.780" | 9.100" | 108.00 in³ | 13.30 in³ | 0.695" | 18.200" | 984.0000 in⁴ | 50.1000 in⁴ | 60.00 lbf/ft | 65.10 ft²/ft | 123.00 in³ | 20.60 in³ | 17.60 in² | W18x60 | 2.1700 in⁴ | 3850.00 in⁶ | 0.405" | 0.415" | 7.560" |
| W18X65 | 0' - 3 1/2" | 3.795" | 9.200" | 117.00 in³ | 14.40 in³ | 0.750" | 18.400" | 1070.0000 in⁴ | 54.8000 in⁴ | 65.00 lbf/ft | 65.60 ft²/ft | 133.00 in³ | 22.50 in³ | 19.10 in² | W18x65 | 2.7300 in⁴ | 4240.00 in⁶ | 0.400" | 0.450" | 7.590" |
| W18X71 | 0' - 3 1/2" | 3.820" | 9.250" | 127.00 in³ | 15.80 in³ | 0.810" | 18.500" | 1170.0000 in⁴ | 60.3000 in⁴ | 71.00 lbf/ft | 65.90 ft²/ft | 146.00 in³ | 24.70 in³ | 20.90 in² | W18x71 | 3.4900 in⁴ | 4700.00 in⁶ | 0.400" | 0.495" | 7.640" |
| W18X76 | 0' - 5 1/2" | 5.500" | 9.100" | 146.00 in³ | 27.60 in³ | 0.680" | 18.200" | 1330.0000 in⁴ | 152.0000 in⁴ | 76.00 lbf/ft | 78.90 ft²/ft | 163.00 in³ | 42.20 in³ | 22.30 in² | W18x76 | 2.8300 in⁴ | 11700.00 in⁶ | 0.400" | 0.425" | 11.000" |
| W18X86 | 0' - 5 1/2" | 5.550" | 9.200" | 166.00 in³ | 31.60 in³ | 0.770" | 18.400" | 1530.0000 in⁴ | 175.0000 in⁴ | 86.00 lbf/ft | 79.50 ft²/ft | 186.00 in³ | 48.40 in³ | 25.30 in² | W18x86 | 4.1000 in⁴ | 13600.00 in⁶ | 0.400" | 0.480" | 11.100" |
| W18X97 | 0' - 5 1/2" | 5.550" | 9.300" | 188.00 in³ | 36.10 in³ | 0.870" | 18.600" | 1750.0000 in⁴ | 201.0000 in⁴ | 97.00 lbf/ft | 79.80 ft²/ft | 211.00 in³ | 55.30 in³ | 28.50 in² | W18x97 | 5.8600 in⁴ | 15800.00 in⁶ | 0.400" | 0.535" | 11.100" |
| W18X106 | 0' - 5 1/2" | 5.600" | 9.350" | 204.00 in³ | 39.40 in³ | 0.940" | 18.700" | 1910.0000 in⁴ | 220.0000 in⁴ | 106.00 lbf/ft | 80.30 ft²/ft | 230.00 in³ | 60.50 in³ | 31.10 in² | W18x106 | 7.4800 in⁴ | 17400.00 in⁶ | 0.400" | 0.590" | 11.200" |
| W18X119 | 0' - 5 1/2" | 5.650" | 9.500" | 231.00 in³ | 44.90 in³ | 1.060" | 19.000" | 2190.0000 in⁴ | 253.0000 in⁴ | 119.00 lbf/ft | 81.20 ft²/ft | 262.00 in³ | 69.10 in³ | 35.10 in² | W18x119 | 10.6000 in⁴ | 20300.00 in⁶ | 0.400" | 0.655" | 11.300" |
| W18X130 | 0' - 5 1/2" | 5.600" | 9.650" | 256.00 in³ | 49.90 in³ | 1.200" | 19.300" | 2460.0000 in⁴ | 278.0000 in⁴ | 130.00 lbf/ft | 81.40 ft²/ft | 290.00 in³ | 76.70 in³ | 38.30 in² | W18x130 | 14.5000 in⁴ | 22700.00 in⁶ | 0.400" | 0.670" | 11.200" |
| W18X143 | 0' - 5 1/2" | 5.600" | 9.750" | 282.00 in³ | 55.50 in³ | 1.320" | 19.500" | 2750.0000 in⁴ | 311.0000 in⁴ | 143.00 lbf/ft | 81.60 ft²/ft | 322.00 in³ | 85.40 in³ | 42.00 in² | W18x143 | 19.2000 in⁴ | 25700.00 in⁶ | 0.400" | 0.730" | 11.200" |
| W18X158 | 0' - 5 1/2" | 5.650" | 9.850" | 310.00 in³ | 61.40 in³ | 1.440" | 19.700" | 3060.0000 in⁴ | 347.0000 in⁴ | 158.00 lbf/ft | 82.30 ft²/ft | 356.00 in³ | 94.80 in³ | 46.30 in² | W18x158 | 25.2000 in⁴ | 29000.00 in⁶ | 0.400" | 0.810" | 11.300" |
| W18X175 | 0' - 5 1/2" | 5.700" | 10.000" | 344.00 in³ | 68.80 in³ | 1.590" | 20.000" | 3450.0000 in⁴ | 391.0000 in⁴ | 175.00 lbf/ft | 83.10 ft²/ft | 398.00 in³ | 106.00 in³ | 51.40 in² | W18x175 | 33.8000 in⁴ | 33300.00 in⁶ | 0.400" | 0.890" | 11.400" |
| W18X192 | 0' - 5 1/2" | 5.750" | 10.200" | 380.00 in³ | 76.80 in³ | 1.750" | 20.400" | 3870.0000 in⁴ | 440.0000 in⁴ | 192.00 lbf/ft | 84.20 ft²/ft | 442.00 in³ | 119.00 in³ | 56.20 in² | W18x192 | 44.7000 in⁴ | 38000.00 in⁶ | 0.400" | 0.960" | 11.500" |
| W18X211 | 0' - 5 1/2" | 5.800" | 10.350" | 419.00 in³ | 85.30 in³ | 1.910" | 20.700" | 4330.0000 in⁴ | 493.0000 in⁴ | 211.00 lbf/ft | 85.00 ft²/ft | 490.00 in³ | 132.00 in³ | 62.30 in² | W18x211 | 58.6000 in⁴ | 43400.00 in⁶ | 0.400" | 1.060" | 11.600" |
| W18X234 | 0' - 5 1/2" | 5.850" | 10.550" | 466.00 in³ | 95.80 in³ | 2.110" | 21.100" | 4900.0000 in⁴ | 558.0000 in⁴ | 234.00 lbf/ft | 86.00 ft²/ft | 549.00 in³ | 149.00 in³ | 68.60 in² | W18x234 | 78.7000 in⁴ | 50100.00 in⁶ | 0.400" | 1.160" | 11.700" |
| W18X258 | 0' - 5 1/2" | 5.900" | 10.750" | 514.00 in³ | 107.00 in³ | 2.300" | 21.500" | 5510.0000 in⁴ | 628.0000 in⁴ | 258.00 lbf/ft | 86.90 ft²/ft | 611.00 in³ | 166.00 in³ | 76.00 in² | W18x258 | 103.0000 in⁴ | 57600.00 in⁶ | 0.400" | 1.280" | 11.800" |
| W18X283 | 0' - 5 1/2" | 5.950" | 10.950" | 565.00 in³ | 118.00 in³ | 2.500" | 21.900" | 6170.0000 in⁴ | 704.0000 in⁴ | 283.00 lbf/ft | 87.70 ft²/ft | 676.00 in³ | 185.00 in³ | 83.30 in² | W18x283 | 134.0000 in⁴ | 65900.00 in⁶ | 0.500" | 1.400" | 11.900" |
| W18X311 | 0' - 5 1/2" | 6.000" | 11.150" | 624.00 in³ | 132.00 in³ | 2.740" | 22.300" | 6970.0000 in⁴ | 795.0000 in⁴ | 311.00 lbf/ft | 88.70 ft²/ft | 754.00 in³ | 207.00 in³ | 91.60 in² | W18x311 | 176.0000 in⁴ | 76200.00 in⁶ | 0.500" | 1.520" | 12.000" |
| W21X44 | 0' - 3 1/2" | 3.250" | 10.350" | 81.60 in³ | 6.37 in³ | 0.450" | 20.700" | 843.0000 in⁴ | 20.7000 in⁴ | 44.00 lbf/ft | 65.80 ft²/ft | 95.40 in³ | 10.20 in³ | 13.00 in² | W21x44 | 0.7700 in⁴ | 2110.00 in⁶ | 0.500" | 0.350" | 6.500" |
| W21X48 | 0' - 5 1/2" | 4.070" | 10.300" | 93.00 in³ | 9.52 in³ | 0.430" | 20.600" | 959.0000 in⁴ | 38.7000 in⁴ | 48.00 lbf/ft | 72.20 ft²/ft | 107.00 in³ | 14.90 in³ | 14.10 in² | W21x48 | 0.8030 in⁴ | 3950.00 in⁶ | 0.500" | 0.350" | 8.140" |
| W21X50 | 0' - 3 1/2" | 3.265" | 10.400" | 94.50 in³ | 7.64 in³ | 0.535" | 20.800" | 984.0000 in⁴ | 24.9000 in⁴ | 50.00 lbf/ft | 66.10 ft²/ft | 110.00 in³ | 12.20 in³ | 14.70 in² | W21x50 | 1.1400 in⁴ | 2570.00 in⁶ | 0.505" | 0.380" | 6.530" |
| W21X55 | 0' - 5 1/2" | 4.110" | 10.400" | 110.00 in³ | 11.80 in³ | 0.522" | 20.800" | 1140.0000 in⁴ | 48.4000 in⁴ | 55.00 lbf/ft | 72.90 ft²/ft | 126.00 in³ | 18.40 in³ | 16.20 in² | W21x55 | 1.2400 in⁴ | 4980.00 in⁶ | 0.498" | 0.375" | 8.220" |
| W21X57 | 0' - 3 1/2" | 3.280" | 10.550" | 111.00 in³ | 9.35 in³ | 0.650" | 21.100" | 1170.0000 in⁴ | 30.6000 in⁴ | 57.00 lbf/ft | 66.80 ft²/ft | 129.00 in³ | 14.80 in³ | 16.70 in² | W21x57 | 1.7700 in⁴ | 3190.00 in⁶ | 0.500" | 0.405" | 6.560" |
| W21X62 | 0' - 5 1/2" | 4.120" | 10.500" | 127.00 in³ | 14.00 in³ | 0.615" | 21.000" | 1330.0000 in⁴ | 57.5000 in⁴ | 62.00 lbf/ft | 73.30 ft²/ft | 144.00 in³ | 21.70 in³ | 18.30 in² | W21x62 | 1.8300 in⁴ | 5960.00 in⁶ | 0.505" | 0.400" | 8.240" |
| W21X68 | 0' - 5 1/2" | 4.135" | 10.550" | 140.00 in³ | 15.70 in³ | 0.685" | 21.100" | 1480.0000 in⁴ | 64.7000 in⁴ | 68.00 lbf/ft | 73.60 ft²/ft | 160.00 in³ | 24.40 in³ | 20.00 in² | W21x68 | 2.4500 in⁴ | 6760.00 in⁶ | 0.505" | 0.430" | 8.270" |
| W21X73 | 0' - 5 1/2" | 4.150" | 10.600" | 151.00 in³ | 17.00 in³ | 0.740" | 21.200" | 1600.0000 in⁴ | 70.6000 in⁴ | 73.00 lbf/ft | 73.80 ft²/ft | 172.00 in³ | 26.60 in³ | 21.50 in² | W21x73 | 3.0200 in⁴ | 7410.00 in⁶ | 0.500" | 0.455" | 8.300" |
| W21X83 | 0' - 5 1/2" | 4.180" | 10.700" | 171.00 in³ | 19.50 in³ | 0.835" | 21.400" | 1830.0000 in⁴ | 81.4000 in⁴ | 83.00 lbf/ft | 74.40 ft²/ft | 196.00 in³ | 30.50 in³ | 24.40 in² | W21x83 | 4.3400 in⁴ | 8630.00 in⁶ | 0.505" | 0.515" | 8.360" |
| W21X93 | 0' - 5 1/2" | 4.210" | 10.800" | 192.00 in³ | 22.10 in³ | 0.930" | 21.600" | 2070.0000 in⁴ | 92.9000 in⁴ | 93.00 lbf/ft | 74.90 ft²/ft | 221.00 in³ | 34.70 in³ | 27.30 in² | W21x93 | 6.0300 in⁴ | 9940.00 in⁶ | 0.500" | 0.580" | 8.420" |
| W21X101 | 0' - 5 1/2" | 6.150" | 10.700" | 227.00 in³ | 40.30 in³ | 0.800" | 21.400" | 2420.0000 in⁴ | 248.0000 in⁴ | 101.00 lbf/ft | 90.10 ft²/ft | 253.00 in³ | 61.70 in³ | 29.80 in² | W21x101 | 5.2100 in⁴ | 26200.00 in⁶ | 0.500" | 0.500" | 12.300" |
| W21X111 | 0' - 5 1/2" | 6.150" | 10.750" | 249.00 in³ | 44.50 in³ | 0.875" | 21.500" | 2670.0000 in⁴ | 274.0000 in⁴ | 111.00 lbf/ft | 90.20 ft²/ft | 279.00 in³ | 68.20 in³ | 32.60 in² | W21x111 | 6.8300 in⁴ | 29200.00 in⁶ | 0.505" | 0.550" | 12.300" |
| W21X122 | 0' - 5 1/2" | 6.200" | 10.850" | 273.00 in³ | 49.20 in³ | 0.960" | 21.700" | 2960.0000 in⁴ | 305.0000 in⁴ | 122.00 lbf/ft | 90.90 ft²/ft | 307.00 in³ | 75.60 in³ | 35.90 in² | W21x122 | 8.9800 in⁴ | 32700.00 in⁶ | 0.500" | 0.600" | 12.400" |
| W21X132 | 0' - 5 1/2" | 6.200" | 10.900" | 295.00 in³ | 53.50 in³ | 1.040" | 21.800" | 3220.0000 in⁴ | 333.0000 in⁴ | 132.00 lbf/ft | 91.00 ft²/ft | 333.00 in³ | 82.30 in³ | 38.80 in² | W21x132 | 11.3000 in⁴ | 36000.00 in⁶ | 0.500" | 0.650" | 12.400" |
| W21X147 | 0' - 5 1/2" | 6.250" | 11.050" | 329.00 in³ | 60.10 in³ | 1.150" | 22.100" | 3630.0000 in⁴ | 376.0000 in⁴ | 147.00 lbf/ft | 91.90 ft²/ft | 373.00 in³ | 92.60 in³ | 43.20 in² | W21x147 | 15.4000 in⁴ | 41100.00 in⁶ | 0.500" | 0.720" | 12.500" |
| W21X166 | 0' - 5 1/2" | 6.200" | 11.250" | 380.00 in³ | 70.00 in³ | 1.360" | 22.500" | 4280.0000 in⁴ | 435.0000 in⁴ | 166.00 lbf/ft | 92.20 ft²/ft | 432.00 in³ | 108.00 in³ | 48.80 in² | W21x166 | 23.6000 in⁴ | 48500.00 in⁶ | 0.500" | 0.750" | 12.400" |
| W21X182 | 0' - 5 1/2" | 6.250" | 11.350" | 417.00 in³ | 77.20 in³ | 1.480" | 22.700" | 4730.0000 in⁴ | 483.0000 in⁴ | 182.00 lbf/ft | 92.90 ft²/ft | 476.00 in³ | 119.00 in³ | 53.60 in² | W21x182 | 30.7000 in⁴ | 54400.00 in⁶ | 0.500" | 0.830" | 12.500" |
| W21X201 | 0' - 5 1/2" | 6.300" | 11.500" | 461.00 in³ | 86.10 in³ | 1.630" | 23.000" | 5310.0000 in⁴ | 542.0000 in⁴ | 201.00 lbf/ft | 93.70 ft²/ft | 530.00 in³ | 133.00 in³ | 59.30 in² | W21x201 | 40.9000 in⁴ | 62000.00 in⁶ | 0.500" | 0.910" | 12.600" |
| W24X55 | 0' - 3 1/2" | 3.505" | 11.800" | 114.00 in³ | 8.30 in³ | 0.505" | 23.600" | 1350.0000 in⁴ | 29.1000 in⁴ | 55.00 lbf/ft | 73.60 ft²/ft | 134.00 in³ | 13.30 in³ | 16.20 in² | W24x55 | 1.1800 in⁴ | 3870.00 in⁶ | 0.505" | 0.395" | 7.010" |
| W24X62 | 0' - 3 1/2" | 3.520" | 11.850" | 131.00 in³ | 9.80 in³ | 0.590" | 23.700" | 1550.0000 in⁴ | 34.5000 in⁴ | 62.00 lbf/ft | 73.80 ft²/ft | 153.00 in³ | 15.70 in³ | 18.20 in² | W24x62 | 1.7100 in⁴ | 4620.00 in⁶ | 0.500" | 0.430" | 7.040" |
| W24X68 | 0' - 5 1/2" | 4.485" | 11.850" | 154.00 in³ | 15.70 in³ | 0.585" | 23.700" | 1830.0000 in⁴ | 70.4000 in⁴ | 68.00 lbf/ft | 81.60 ft²/ft | 177.00 in³ | 24.50 in³ | 20.10 in² | W24x68 | 1.8700 in⁴ | 9430.00 in⁶ | 0.505" | 0.415" | 8.970" |
| W24X76 | 0' - 5 1/2" | 4.495" | 11.950" | 176.00 in³ | 18.40 in³ | 0.680" | 23.900" | 2100.0000 in⁴ | 82.5000 in⁴ | 76.00 lbf/ft | 82.00 ft²/ft | 200.00 in³ | 28.60 in³ | 22.40 in² | W24x76 | 2.6800 in⁴ | 11100.00 in⁶ | 0.500" | 0.440" | 8.990" |
| W24X84 | 0' - 5 1/2" | 4.510" | 12.050" | 196.00 in³ | 20.90 in³ | 0.770" | 24.100" | 2370.0000 in⁴ | 94.4000 in⁴ | 84.00 lbf/ft | 82.50 ft²/ft | 224.00 in³ | 32.60 in³ | 24.70 in² | W24x84 | 3.7000 in⁴ | 12800.00 in⁶ | 0.500" | 0.470" | 9.020" |
| W24X94 | 0' - 5 1/2" | 4.535" | 12.150" | 222.00 in³ | 24.00 in³ | 0.875" | 24.300" | 2700.0000 in⁴ | 109.0000 in⁴ | 94.00 lbf/ft | 83.00 ft²/ft | 254.00 in³ | 37.50 in³ | 27.70 in² | W24x94 | 5.2600 in⁴ | 15000.00 in⁶ | 0.505" | 0.515" | 9.070" |
| W24X103 | 0' - 5 1/2" | 4.500" | 12.250" | 245.00 in³ | 26.50 in³ | 0.980" | 24.500" | 3000.0000 in⁴ | 119.0000 in⁴ | 103.00 lbf/ft | 83.00 ft²/ft | 280.00 in³ | 41.50 in³ | 30.30 in² | W24x103 | 7.0700 in⁴ | 16600.00 in⁶ | 0.500" | 0.550" | 9.000" |
| W24X104 | 0' - 5 1/2" | 6.400" | 12.050" | 258.00 in³ | 40.70 in³ | 0.750" | 24.100" | 3100.0000 in⁴ | 259.0000 in⁴ | 104.00 lbf/ft | 97.50 ft²/ft | 289.00 in³ | 62.40 in³ | 30.70 in² | W24x104 | 4.7200 in⁴ | 35200.00 in⁶ | 0.500" | 0.500" | 12.800" |
| W24X117 | 0' - 5 1/2" | 6.400" | 12.150" | 291.00 in³ | 46.50 in³ | 0.850" | 24.300" | 3540.0000 in⁴ | 297.0000 in⁴ | 117.00 lbf/ft | 97.80 ft²/ft | 327.00 in³ | 71.40 in³ | 34.40 in² | W24x117 | 6.7200 in⁴ | 40800.00 in⁶ | 0.500" | 0.550" | 12.800" |
| W24X131 | 0' - 5 1/2" | 6.450" | 12.250" | 329.00 in³ | 53.00 in³ | 0.960" | 24.500" | 4020.0000 in⁴ | 340.0000 in⁴ | 131.00 lbf/ft | 98.50 ft²/ft | 370.00 in³ | 81.50 in³ | 38.60 in² | W24x131 | 9.5000 in⁴ | 47100.00 in⁶ | 0.500" | 0.605" | 12.900" |
| W24X146 | 0' - 5 1/2" | 6.450" | 12.350" | 371.00 in³ | 60.50 in³ | 1.090" | 24.700" | 4580.0000 in⁴ | 391.0000 in⁴ | 146.00 lbf/ft | 98.80 ft²/ft | 418.00 in³ | 93.20 in³ | 43.00 in² | W24x146 | 13.4000 in⁴ | 54600.00 in⁶ | 0.500" | 0.650" | 12.900" |
| W24X162 | 0' - 5 1/2" | 6.500" | 12.500" | 414.00 in³ | 68.40 in³ | 1.220" | 25.000" | 5170.0000 in⁴ | 443.0000 in⁴ | 162.00 lbf/ft | 99.70 ft²/ft | 468.00 in³ | 105.00 in³ | 47.80 in² | W24x162 | 18.5000 in⁴ | 62600.00 in⁶ | 0.500" | 0.705" | 13.000" |
| W24X176 | 0' - 5 1/2" | 6.450" | 12.600" | 450.00 in³ | 74.30 in³ | 1.340" | 25.200" | 5680.0000 in⁴ | 479.0000 in⁴ | 176.00 lbf/ft | 99.60 ft²/ft | 511.00 in³ | 115.00 in³ | 51.70 in² | W24x176 | 23.9000 in⁴ | 68400.00 in⁶ | 0.500" | 0.750" | 12.900" |
| W24X192 | 0' - 5 1/2" | 6.500" | 12.750" | 491.00 in³ | 81.80 in³ | 1.460" | 25.500" | 6260.0000 in⁴ | 530.0000 in⁴ | 192.00 lbf/ft | 101.00 ft²/ft | 559.00 in³ | 126.00 in³ | 56.50 in² | W24x192 | 30.8000 in⁴ | 76300.00 in⁶ | 0.500" | 0.810" | 13.000" |
| W24X207 | 0' - 5 1/2" | 6.500" | 12.850" | 531.00 in³ | 88.80 in³ | 1.570" | 25.700" | 6820.0000 in⁴ | 578.0000 in⁴ | 207.00 lbf/ft | 101.00 ft²/ft | 606.00 in³ | 137.00 in³ | 60.70 in² | W24x207 | 38.3000 in⁴ | 84100.00 in⁶ | 0.500" | 0.870" | 13.000" |
| W24X229 | 0' - 5 1/2" | 6.550" | 13.000" | 588.00 in³ | 99.40 in³ | 1.730" | 26.000" | 7650.0000 in⁴ | 651.0000 in⁴ | 229.00 lbf/ft | 102.00 ft²/ft | 675.00 in³ | 154.00 in³ | 67.20 in² | W24x229 | 51.3000 in⁴ | 96100.00 in⁶ | 0.500" | 0.960" | 13.100" |
| W24X250 | 0' - 5 1/2" | 6.600" | 13.150" | 644.00 in³ | 110.00 in³ | 1.890" | 26.300" | 8490.0000 in⁴ | 724.0000 in⁴ | 250.00 lbf/ft | 102.00 ft²/ft | 744.00 in³ | 171.00 in³ | 73.50 in² | W24x250 | 66.6000 in⁴ | 108000.00 in⁶ | 0.500" | 1.040" | 13.200" |
| W24X279 | 0' - 5 1/2" | 6.650" | 13.350" | 718.00 in³ | 124.00 in³ | 2.090" | 26.700" | 9600.0000 in⁴ | 823.0000 in⁴ | 279.00 lbf/ft | 103.00 ft²/ft | 835.00 in³ | 193.00 in³ | 81.90 in² | W24x279 | 90.5000 in⁴ | 125000.00 in⁶ | 0.500" | 1.160" | 13.300" |
| W24X306 | 0' - 5 1/2" | 6.700" | 13.550" | 789.00 in³ | 137.00 in³ | 2.280" | 27.100" | 10700.0000 in⁴ | 919.0000 in⁴ | 306.00 lbf/ft | 104.00 ft²/ft | 922.00 in³ | 214.00 in³ | 89.70 in² | W24x306 | 117.0000 in⁴ | 142000.00 in⁶ | 0.500" | 1.260" | 13.400" |
| W24X335 | 0' - 5 1/2" | 6.750" | 13.750" | 864.00 in³ | 152.00 in³ | 2.480" | 27.500" | 11900.0000 in⁴ | 1030.0000 in⁴ | 335.00 lbf/ft | 105.00 ft²/ft | 1020.00 in³ | 238.00 in³ | 98.30 in² | W24x335 | 152.0000 in⁴ | 161000.00 in⁶ | 0.500" | 1.380" | 13.500" |
| W24X370 | 0' - 5 1/2" | 6.850" | 14.000" | 957.00 in³ | 170.00 in³ | 2.720" | 28.000" | 13400.0000 in⁴ | 1160.0000 in⁴ | 370.00 lbf/ft | 107.00 ft²/ft | 1130.00 in³ | 267.00 in³ | 109.00 in² | W24x370 | 201.0000 in⁴ | 186000.00 in⁶ | 0.500" | 1.520" | 13.700" |
| W27X84 | 0' - 5 1/2" | 5.000" | 13.350" | 213.00 in³ | 21.20 in³ | 0.640" | 26.700" | 2850.0000 in⁴ | 106.0000 in⁴ | 84.00 lbf/ft | 91.50 ft²/ft | 244.00 in³ | 33.20 in³ | 24.70 in² | W27x84 | 2.8100 in⁴ | 17900.00 in⁶ | 0.600" | 0.460" | 10.000" |
| W27X94 | 0' - 5 1/2" | 5.000" | 13.450" | 243.00 in³ | 24.80 in³ | 0.745" | 26.900" | 3270.0000 in⁴ | 124.0000 in⁴ | 94.00 lbf/ft | 91.80 ft²/ft | 278.00 in³ | 38.80 in³ | 27.60 in² | W27x94 | 4.0300 in⁴ | 21300.00 in⁶ | 0.595" | 0.490" | 10.000" |
| W27X102 | 0' - 5 1/2" | 5.000" | 13.550" | 267.00 in³ | 27.80 in³ | 0.830" | 27.100" | 3620.0000 in⁴ | 139.0000 in⁴ | 102.00 lbf/ft | 92.10 ft²/ft | 305.00 in³ | 43.40 in³ | 30.00 in² | W27x102 | 5.2800 in⁴ | 24000.00 in⁶ | 0.600" | 0.515" | 10.000" |
| W27X114 | 0' - 5 1/2" | 5.050" | 13.650" | 299.00 in³ | 31.50 in³ | 0.930" | 27.300" | 4080.0000 in⁴ | 159.0000 in⁴ | 114.00 lbf/ft | 92.80 ft²/ft | 343.00 in³ | 49.30 in³ | 33.60 in² | W27x114 | 7.3300 in⁴ | 27600.00 in⁶ | 0.600" | 0.570" | 10.100" |
| W27X129 | 0' - 5 1/2" | 5.000" | 13.800" | 345.00 in³ | 36.80 in³ | 1.100" | 27.600" | 4760.0000 in⁴ | 184.0000 in⁴ | 129.00 lbf/ft | 93.00 ft²/ft | 395.00 in³ | 57.60 in³ | 37.80 in² | W27x129 | 11.1000 in⁴ | 32500.00 in⁶ | 0.600" | 0.610" | 10.000" |
| W27X146 | 0' - 5 1/2" | 7.000" | 13.700" | 414.00 in³ | 63.50 in³ | 0.975" | 27.400" | 5660.0000 in⁴ | 443.0000 in⁴ | 146.00 lbf/ft | 108.00 ft²/ft | 464.00 in³ | 97.70 in³ | 43.20 in² | W27x146 | 11.3000 in⁴ | 77200.00 in⁶ | 0.785" | 0.605" | 14.000" |
| W27X161 | 0' - 5 1/2" | 7.000" | 13.800" | 458.00 in³ | 70.90 in³ | 1.080" | 27.600" | 6310.0000 in⁴ | 497.0000 in⁴ | 161.00 lbf/ft | 109.00 ft²/ft | 515.00 in³ | 109.00 in³ | 47.60 in² | W27x161 | 15.1000 in⁴ | 87300.00 in⁶ | 0.790" | 0.660" | 14.000" |
| W27X178 | 0' - 5 1/2" | 7.050" | 13.900" | 505.00 in³ | 78.80 in³ | 1.190" | 27.800" | 7020.0000 in⁴ | 555.0000 in⁴ | 178.00 lbf/ft | 109.00 ft²/ft | 570.00 in³ | 122.00 in³ | 52.50 in² | W27x178 | 20.1000 in⁴ | 98400.00 in⁶ | 0.790" | 0.725" | 14.100" |
| W27X194 | 0' - 5 1/2" | 7.000" | 14.050" | 559.00 in³ | 88.10 in³ | 1.340" | 28.100" | 7860.0000 in⁴ | 619.0000 in⁴ | 194.00 lbf/ft | 109.00 ft²/ft | 631.00 in³ | 136.00 in³ | 57.10 in² | W27x194 | 27.1000 in⁴ | 111000.00 in⁶ | 0.790" | 0.750" | 14.000" |
| W27X217 | 0' - 5 1/2" | 7.050" | 14.200" | 627.00 in³ | 100.00 in³ | 1.500" | 28.400" | 8910.0000 in⁴ | 704.0000 in⁴ | 217.00 lbf/ft | 110.00 ft²/ft | 711.00 in³ | 154.00 in³ | 63.90 in² | W27x217 | 37.6000 in⁴ | 128000.00 in⁶ | 0.790" | 0.830" | 14.100" |
| W27X235 | 0' - 5 1/2" | 7.100" | 14.350" | 677.00 in³ | 108.00 in³ | 1.610" | 28.700" | 9700.0000 in⁴ | 769.0000 in⁴ | 235.00 lbf/ft | 111.00 ft²/ft | 772.00 in³ | 168.00 in³ | 69.40 in² | W27x235 | 47.0000 in⁴ | 141000.00 in⁶ | 0.790" | 0.910" | 14.200" |
| W27X258 | 0' - 5 1/2" | 7.150" | 14.500" | 745.00 in³ | 120.00 in³ | 1.770" | 29.000" | 10800.0000 in⁴ | 859.0000 in⁴ | 258.00 lbf/ft | 112.00 ft²/ft | 852.00 in³ | 187.00 in³ | 76.10 in² | W27x258 | 61.6000 in⁴ | 159000.00 in⁶ | 0.790" | 0.980" | 14.300" |
| W27X281 | 0' - 5 1/2" | 7.200" | 14.650" | 814.00 in³ | 133.00 in³ | 1.930" | 29.300" | 11900.0000 in⁴ | 953.0000 in⁴ | 281.00 lbf/ft | 113.00 ft²/ft | 936.00 in³ | 206.00 in³ | 83.10 in² | W27x281 | 79.5000 in⁴ | 178000.00 in⁶ | 0.790" | 1.060" | 14.400" |
| W27X307 | 0' - 5 1/2" | 7.200" | 14.800" | 887.00 in³ | 146.00 in³ | 2.090" | 29.600" | 13100.0000 in⁴ | 1050.0000 in⁴ | 307.00 lbf/ft | 113.00 ft²/ft | 1030.00 in³ | 227.00 in³ | 90.20 in² | W27x307 | 101.0000 in⁴ | 199000.00 in⁶ | 0.790" | 1.160" | 14.400" |
| W27X336 | 0' - 5 1/2" | 7.300" | 15.000" | 972.00 in³ | 162.00 in³ | 2.280" | 30.000" | 14600.0000 in⁴ | 1180.0000 in⁴ | 336.00 lbf/ft | 115.00 ft²/ft | 1130.00 in³ | 252.00 in³ | 99.20 in² | W27x336 | 131.0000 in⁴ | 226000.00 in⁶ | 0.790" | 1.260" | 14.600" |
| W27X368 | 0' - 5 1/2" | 7.350" | 15.200" | 1060.00 in³ | 179.00 in³ | 2.480" | 30.400" | 16200.0000 in⁴ | 1310.0000 in⁴ | 368.00 lbf/ft | 115.00 ft²/ft | 1240.00 in³ | 279.00 in³ | 109.00 in² | W27x368 | 170.0000 in⁴ | 255000.00 in⁶ | 0.790" | 1.380" | 14.700" |
| W27X539 | 0' - 5 1/2" | 7.650" | 16.250" | 1570.00 in³ | 277.00 in³ | 3.540" | 32.500" | 25600.0000 in⁴ | 2110.0000 in⁴ | 539.00 lbf/ft | 121.00 ft²/ft | 1890.00 in³ | 437.00 in³ | 159.00 in² | W27x539 | 496.0000 in⁴ | 443000.00 in⁶ | 0.790" | 1.970" | 15.300" |
| W30X90 | 0' - 5 1/2" | 5.200" | 14.750" | 245.00 in³ | 22.10 in³ | 0.610" | 29.500" | 3610.0000 in⁴ | 115.0000 in⁴ | 90.00 lbf/ft | 98.50 ft²/ft | 283.00 in³ | 34.70 in³ | 26.30 in² | W30x90 | 2.8400 in⁴ | 24000.00 in⁶ | 0.650" | 0.470" | 10.400" |
| W30X99 | 0' - 5 1/2" | 5.250" | 14.850" | 269.00 in³ | 24.50 in³ | 0.670" | 29.700" | 3990.0000 in⁴ | 128.0000 in⁴ | 99.00 lbf/ft | 99.20 ft²/ft | 312.00 in³ | 38.60 in³ | 29.00 in² | W30x99 | 3.7700 in⁴ | 26800.00 in⁶ | 0.650" | 0.520" | 10.500" |
| W30X108 | 0' - 5 1/2" | 5.250" | 14.900" | 299.00 in³ | 27.90 in³ | 0.760" | 29.800" | 4470.0000 in⁴ | 146.0000 in⁴ | 108.00 lbf/ft | 99.40 ft²/ft | 346.00 in³ | 43.90 in³ | 31.70 in² | W30x108 | 4.9900 in⁴ | 30900.00 in⁶ | 0.650" | 0.545" | 10.500" |
| W30X116 | 0' - 5 1/2" | 5.250" | 15.000" | 329.00 in³ | 31.30 in³ | 0.850" | 30.000" | 4930.0000 in⁴ | 164.0000 in⁴ | 116.00 lbf/ft | 99.80 ft²/ft | 378.00 in³ | 49.20 in³ | 34.20 in² | W30x116 | 6.4300 in⁴ | 34900.00 in⁶ | 0.650" | 0.565" | 10.500" |
| W30X124 | 0' - 5 1/2" | 5.250" | 15.100" | 355.00 in³ | 34.40 in³ | 0.930" | 30.200" | 5360.0000 in⁴ | 181.0000 in⁴ | 124.00 lbf/ft | 100.00 ft²/ft | 408.00 in³ | 54.00 in³ | 36.50 in² | W30x124 | 7.9900 in⁴ | 38600.00 in⁶ | 0.650" | 0.585" | 10.500" |
| W30X132 | 0' - 5 1/2" | 5.250" | 15.150" | 380.00 in³ | 37.20 in³ | 1.000" | 30.300" | 5770.0000 in⁴ | 196.0000 in⁴ | 132.00 lbf/ft | 100.00 ft²/ft | 437.00 in³ | 58.40 in³ | 38.80 in² | W30x132 | 9.7200 in⁴ | 42100.00 in⁶ | 0.650" | 0.615" | 10.500" |
| W30X148 | 0' - 5 1/2" | 5.250" | 15.350" | 436.00 in³ | 43.30 in³ | 1.180" | 30.700" | 6680.0000 in⁴ | 227.0000 in⁴ | 148.00 lbf/ft | 101.00 ft²/ft | 500.00 in³ | 68.00 in³ | 43.60 in² | W30x148 | 14.5000 in⁴ | 49400.00 in⁶ | 0.650" | 0.650" | 10.500" |
| W30X173 | 0' - 5 1/2" | 7.500" | 15.200" | 541.00 in³ | 79.80 in³ | 1.070" | 30.400" | 8230.0000 in⁴ | 598.0000 in⁴ | 173.00 lbf/ft | 118.00 ft²/ft | 607.00 in³ | 123.00 in³ | 50.90 in² | W30x173 | 15.6000 in⁴ | 129000.00 in⁶ | 0.780" | 0.655" | 15.000" |
| W30X191 | 0' - 5 1/2" | 7.500" | 15.350" | 600.00 in³ | 89.50 in³ | 1.190" | 30.700" | 9200.0000 in⁴ | 673.0000 in⁴ | 191.00 lbf/ft | 119.00 ft²/ft | 675.00 in³ | 138.00 in³ | 56.10 in² | W30x191 | 21.0000 in⁴ | 146000.00 in⁶ | 0.780" | 0.710" | 15.000" |
| W30X211 | 0' - 5 1/2" | 7.550" | 15.450" | 665.00 in³ | 100.00 in³ | 1.320" | 30.900" | 10300.0000 in⁴ | 757.0000 in⁴ | 211.00 lbf/ft | 119.00 ft²/ft | 751.00 in³ | 155.00 in³ | 62.30 in² | W30x211 | 28.4000 in⁴ | 166000.00 in⁶ | 0.780" | 0.775" | 15.100" |
| W30X235 | 0' - 5 1/2" | 7.550" | 15.650" | 748.00 in³ | 114.00 in³ | 1.500" | 31.300" | 11700.0000 in⁴ | 855.0000 in⁴ | 235.00 lbf/ft | 120.00 ft²/ft | 847.00 in³ | 175.00 in³ | 69.30 in² | W30x235 | 40.3000 in⁴ | 190000.00 in⁶ | 0.790" | 0.830" | 15.100" |
| W30X261 | 0' - 5 1/2" | 7.600" | 15.800" | 829.00 in³ | 127.00 in³ | 1.650" | 31.600" | 13100.0000 in⁴ | 959.0000 in⁴ | 261.00 lbf/ft | 121.00 ft²/ft | 943.00 in³ | 196.00 in³ | 77.00 in² | W30x261 | 54.1000 in⁴ | 215000.00 in⁶ | 0.790" | 0.930" | 15.200" |
| W30X292 | 0' - 5 1/2" | 7.650" | 16.000" | 930.00 in³ | 144.00 in³ | 1.850" | 32.000" | 14900.0000 in⁴ | 1100.0000 in⁴ | 292.00 lbf/ft | 122.00 ft²/ft | 1060.00 in³ | 223.00 in³ | 86.00 in² | W30x292 | 75.2000 in⁴ | 250000.00 in⁶ | 0.790" | 1.020" | 15.300" |
| W30X326 | 0' - 5 1/2" | 7.700" | 16.200" | 1040.00 in³ | 162.00 in³ | 2.050" | 32.400" | 16800.0000 in⁴ | 1240.0000 in⁴ | 326.00 lbf/ft | 123.00 ft²/ft | 1190.00 in³ | 252.00 in³ | 95.90 in² | W30x326 | 103.0000 in⁴ | 287000.00 in⁶ | 0.790" | 1.140" | 15.400" |
| W30X357 | 0' - 5 1/2" | 7.750" | 16.400" | 1140.00 in³ | 179.00 in³ | 2.240" | 32.800" | 18700.0000 in⁴ | 1390.0000 in⁴ | 357.00 lbf/ft | 124.00 ft²/ft | 1320.00 in³ | 279.00 in³ | 105.00 in² | W30x357 | 134.0000 in⁴ | 324000.00 in⁶ | 0.790" | 1.240" | 15.500" |
| W30X391 | 0' - 5 1/2" | 7.800" | 16.600" | 1250.00 in³ | 198.00 in³ | 2.440" | 33.200" | 20700.0000 in⁴ | 1550.0000 in⁴ | 391.00 lbf/ft | 125.00 ft²/ft | 1450.00 in³ | 310.00 in³ | 115.00 in² | W30x391 | 173.0000 in⁴ | 366000.00 in⁶ | 0.790" | 1.360" | 15.600" |
| W33X118 | 0' - 5 1/2" | 5.750" | 16.450" | 359.00 in³ | 32.60 in³ | 0.740" | 32.900" | 5900.0000 in⁴ | 187.0000 in⁴ | 118.00 lbf/ft | 109.00 ft²/ft | 415.00 in³ | 51.30 in³ | 34.70 in² | W33x118 | 5.3000 in⁴ | 48300.00 in⁶ | 0.700" | 0.550" | 11.500" |
| W33X130 | 0' - 5 1/2" | 5.750" | 16.550" | 406.00 in³ | 37.90 in³ | 0.855" | 33.100" | 6710.0000 in⁴ | 218.0000 in⁴ | 130.00 lbf/ft | 110.00 ft²/ft | 467.00 in³ | 59.50 in³ | 38.30 in² | W33x130 | 7.3700 in⁴ | 56600.00 in⁶ | 0.705" | 0.580" | 11.500" |
| W33X141 | 0' - 5 1/2" | 5.750" | 16.650" | 448.00 in³ | 42.70 in³ | 0.960" | 33.300" | 7450.0000 in⁴ | 246.0000 in⁴ | 141.00 lbf/ft | 110.00 ft²/ft | 514.00 in³ | 66.90 in³ | 41.50 in² | W33x141 | 9.7000 in⁴ | 64400.00 in⁶ | 0.700" | 0.605" | 11.500" |
| W33X152 | 0' - 5 1/2" | 5.800" | 16.750" | 487.00 in³ | 47.20 in³ | 1.060" | 33.500" | 8160.0000 in⁴ | 273.0000 in⁴ | 152.00 lbf/ft | 111.00 ft²/ft | 559.00 in³ | 73.90 in³ | 44.90 in² | W33x152 | 12.4000 in⁴ | 71700.00 in⁶ | 0.700" | 0.635" | 11.600" |
| W33X169 | 0' - 5 1/2" | 5.750" | 16.900" | 549.00 in³ | 53.90 in³ | 1.220" | 33.800" | 9290.0000 in⁴ | 310.0000 in⁴ | 169.00 lbf/ft | 111.00 ft²/ft | 629.00 in³ | 84.40 in³ | 49.50 in² | W33x169 | 17.7000 in⁴ | 82400.00 in⁶ | 0.700" | 0.670" | 11.500" |
| W33X201 | 0' - 5 1/2" | 7.850" | 16.850" | 686.00 in³ | 95.20 in³ | 1.150" | 33.700" | 11600.0000 in⁴ | 749.0000 in⁴ | 201.00 lbf/ft | 127.00 ft²/ft | 773.00 in³ | 147.00 in³ | 59.10 in² | W33x201 | 20.8000 in⁴ | 198000.00 in⁶ | 0.790" | 0.715" | 15.700" |
| W33X221 | 0' - 5 1/2" | 7.900" | 16.950" | 759.00 in³ | 106.00 in³ | 1.280" | 33.900" | 12900.0000 in⁴ | 840.0000 in⁴ | 221.00 lbf/ft | 128.00 ft²/ft | 857.00 in³ | 164.00 in³ | 65.30 in² | W33x221 | 27.8000 in⁴ | 224000.00 in⁶ | 0.780" | 0.775" | 15.800" |
| W33X241 | 0' - 5 1/2" | 7.950" | 17.100" | 831.00 in³ | 118.00 in³ | 1.400" | 34.200" | 14200.0000 in⁴ | 933.0000 in⁴ | 241.00 lbf/ft | 129.00 ft²/ft | 940.00 in³ | 182.00 in³ | 71.10 in² | W33x241 | 36.2000 in⁴ | 251000.00 in⁶ | 0.790" | 0.830" | 15.900" |
| W33X263 | 0' - 5 1/2" | 7.900" | 17.250" | 919.00 in³ | 131.00 in³ | 1.570" | 34.500" | 15900.0000 in⁴ | 1040.0000 in⁴ | 263.00 lbf/ft | 129.00 ft²/ft | 1040.00 in³ | 202.00 in³ | 77.40 in² | W33x263 | 48.7000 in⁴ | 281000.00 in⁶ | 0.790" | 0.870" | 15.800" |
| W33X291 | 0' - 5 1/2" | 7.950" | 17.400" | 1020.00 in³ | 146.00 in³ | 1.730" | 34.800" | 17700.0000 in⁴ | 1160.0000 in⁴ | 291.00 lbf/ft | 130.00 ft²/ft | 1160.00 in³ | 226.00 in³ | 85.60 in² | W33x291 | 65.1000 in⁴ | 319000.00 in⁶ | 0.790" | 0.960" | 15.900" |
| W33X318 | 0' - 5 1/2" | 8.000" | 17.600" | 1110.00 in³ | 161.00 in³ | 1.890" | 35.200" | 19500.0000 in⁴ | 1290.0000 in⁴ | 318.00 lbf/ft | 131.00 ft²/ft | 1270.00 in³ | 250.00 in³ | 93.70 in² | W33x318 | 84.4000 in⁴ | 357000.00 in⁶ | 0.790" | 1.040" | 16.000" |
| W33X354 | 0' - 5 1/2" | 8.050" | 17.800" | 1240.00 in³ | 181.00 in³ | 2.090" | 35.600" | 22000.0000 in⁴ | 1460.0000 in⁴ | 354.00 lbf/ft | 132.00 ft²/ft | 1420.00 in³ | 282.00 in³ | 104.00 in² | W33x354 | 115.0000 in⁴ | 408000.00 in⁶ | 0.790" | 1.160" | 16.100" |
| W33X387 | 0' - 5 1/2" | 8.100" | 18.000" | 1350.00 in³ | 200.00 in³ | 2.280" | 36.000" | 24300.0000 in⁴ | 1620.0000 in⁴ | 387.00 lbf/ft | 133.00 ft²/ft | 1560.00 in³ | 312.00 in³ | 114.00 in² | W33x387 | 148.0000 in⁴ | 459000.00 in⁶ | 0.790" | 1.260" | 16.200" |
| W36X135 | 0' - 5 1/2" | 6.000" | 17.800" | 439.00 in³ | 37.70 in³ | 0.790" | 35.600" | 7800.0000 in⁴ | 225.0000 in⁴ | 135.00 lbf/ft | 117.00 ft²/ft | 509.00 in³ | 59.70 in³ | 39.90 in² | W36x135 | 7.0000 in⁴ | 68100.00 in⁶ | 0.750" | 0.600" | 12.000" |
| W36X150 | 0' - 5 1/2" | 6.000" | 17.950" | 504.00 in³ | 45.10 in³ | 0.940" | 35.900" | 9040.0000 in⁴ | 270.0000 in⁴ | 150.00 lbf/ft | 117.00 ft²/ft | 581.00 in³ | 70.90 in³ | 44.30 in² | W36x150 | 10.1000 in⁴ | 82200.00 in⁶ | 0.750" | 0.625" | 12.000" |
| W36X160 | 0' - 5 1/2" | 6.000" | 18.000" | 542.00 in³ | 49.10 in³ | 1.020" | 36.000" | 9760.0000 in⁴ | 295.0000 in⁴ | 160.00 lbf/ft | 117.00 ft²/ft | 624.00 in³ | 77.30 in³ | 47.00 in² | W36x160 | 12.4000 in⁴ | 90200.00 in⁶ | 0.750" | 0.650" | 12.000" |
| W36X170 | 0' - 5 1/2" | 6.000" | 18.100" | 581.00 in³ | 53.20 in³ | 1.100" | 36.200" | 10500.0000 in⁴ | 320.0000 in⁴ | 170.00 lbf/ft | 118.00 ft²/ft | 668.00 in³ | 83.80 in³ | 50.00 in² | W36x170 | 15.1000 in⁴ | 98500.00 in⁶ | 0.750" | 0.680" | 12.000" |
| W36X182 | 0' - 5 1/2" | 6.050" | 18.150" | 623.00 in³ | 57.60 in³ | 1.180" | 36.300" | 11300.0000 in⁴ | 347.0000 in⁴ | 182.00 lbf/ft | 118.00 ft²/ft | 718.00 in³ | 90.70 in³ | 53.60 in² | W36x182 | 18.5000 in⁴ | 107000.00 in⁶ | 0.750" | 0.725" | 12.100" |
| W36X194 | 0' - 5 1/2" | 6.050" | 18.250" | 664.00 in³ | 61.90 in³ | 1.260" | 36.500" | 12100.0000 in⁴ | 375.0000 in⁴ | 194.00 lbf/ft | 119.00 ft²/ft | 767.00 in³ | 97.70 in³ | 57.00 in² | W36x194 | 22.2000 in⁴ | 116000.00 in⁶ | 0.750" | 0.765" | 12.100" |
| W36X210 | 0' - 5 1/2" | 6.100" | 18.350" | 719.00 in³ | 67.50 in³ | 1.360" | 36.700" | 13200.0000 in⁴ | 411.0000 in⁴ | 210.00 lbf/ft | 119.00 ft²/ft | 833.00 in³ | 107.00 in³ | 61.90 in² | W36x210 | 28.0000 in⁴ | 128000.00 in⁶ | 0.750" | 0.830" | 12.200" |
| W36X231 | 0' - 7 1/2" | 8.250" | 18.250" | 854.00 in³ | 114.00 in³ | 1.260" | 36.500" | 15600.0000 in⁴ | 940.0000 in⁴ | 231.00 lbf/ft | 136.00 ft²/ft | 963.00 in³ | 176.00 in³ | 68.20 in² | W36x231 | 28.7000 in⁴ | 292000.00 in⁶ | 0.950" | 0.760" | 16.500" |
| W36X232 | 0' - 5 1/2" | 6.050" | 18.550" | 809.00 in³ | 77.20 in³ | 1.570" | 37.100" | 15000.0000 in⁴ | 468.0000 in⁴ | 232.00 lbf/ft | 120.00 ft²/ft | 936.00 in³ | 122.00 in³ | 68.00 in² | W36x232 | 39.6000 in⁴ | 148000.00 in⁶ | 0.750" | 0.870" | 12.100" |
| W36X247 | 0' - 7 1/2" | 8.250" | 18.350" | 913.00 in³ | 123.00 in³ | 1.350" | 36.700" | 16700.0000 in⁴ | 1010.0000 in⁴ | 247.00 lbf/ft | 136.00 ft²/ft | 1030.00 in³ | 190.00 in³ | 72.50 in² | W36x247 | 34.7000 in⁴ | 316000.00 in⁶ | 0.950" | 0.800" | 16.500" |
| W36X256 | 0' - 5 1/2" | 6.100" | 18.700" | 895.00 in³ | 86.50 in³ | 1.730" | 37.400" | 16800.0000 in⁴ | 528.0000 in⁴ | 256.00 lbf/ft | 120.00 ft²/ft | 1040.00 in³ | 137.00 in³ | 75.30 in² | W36x256 | 52.9000 in⁴ | 168000.00 in⁶ | 0.750" | 0.960" | 12.200" |
| W36X262 | 0' - 7 1/2" | 8.300" | 18.450" | 972.00 in³ | 132.00 in³ | 1.440" | 36.900" | 17900.0000 in⁴ | 1090.0000 in⁴ | 262.00 lbf/ft | 137.00 ft²/ft | 1100.00 in³ | 204.00 in³ | 77.20 in² | W36x262 | 41.6000 in⁴ | 342000.00 in⁶ | 0.950" | 0.840" | 16.600" |
| W36X282 | 0' - 7 1/2" | 8.300" | 18.550" | 1050.00 in³ | 144.00 in³ | 1.570" | 37.100" | 19600.0000 in⁴ | 1200.0000 in⁴ | 282.00 lbf/ft | 137.00 ft²/ft | 1190.00 in³ | 223.00 in³ | 82.90 in² | W36x282 | 52.7000 in⁴ | 378000.00 in⁶ | 0.950" | 0.885" | 16.600" |
| W36X302 | 0' - 7 1/2" | 8.350" | 18.650" | 1130.00 in³ | 156.00 in³ | 1.680" | 37.300" | 21100.0000 in⁴ | 1300.0000 in⁴ | 302.00 lbf/ft | 138.00 ft²/ft | 1280.00 in³ | 241.00 in³ | 89.00 in² | W36x302 | 64.3000 in⁴ | 412000.00 in⁶ | 0.950" | 0.945" | 16.700" |
| W36X330 | 0' - 7 1/2" | 8.300" | 18.850" | 1240.00 in³ | 171.00 in³ | 1.850" | 37.700" | 23300.0000 in⁴ | 1420.0000 in⁴ | 330.00 lbf/ft | 138.00 ft²/ft | 1410.00 in³ | 265.00 in³ | 96.90 in² | W36x330 | 84.3000 in⁴ | 456000.00 in⁶ | 0.950" | 1.020" | 16.600" |
| W36X361 | 0' - 7 1/2" | 8.350" | 19.000" | 1350.00 in³ | 188.00 in³ | 2.010" | 38.000" | 25700.0000 in⁴ | 1570.0000 in⁴ | 361.00 lbf/ft | 139.00 ft²/ft | 1550.00 in³ | 293.00 in³ | 106.00 in² | W36x361 | 109.0000 in⁴ | 509000.00 in⁶ | 0.950" | 1.120" | 16.700" |
| W36X395 | 0' - 7 1/2" | 8.400" | 19.200" | 1490.00 in³ | 208.00 in³ | 2.200" | 38.400" | 28500.0000 in⁴ | 1750.0000 in⁴ | 395.00 lbf/ft | 140.00 ft²/ft | 1710.00 in³ | 325.00 in³ | 116.00 in² | W36x395 | 142.0000 in⁴ | 575000.00 in⁶ | 0.950" | 1.220" | 16.800" |
| W36X441 | 0' - 7 1/2" | 8.500" | 19.450" | 1650.00 in³ | 235.00 in³ | 2.440" | 38.900" | 32100.0000 in⁴ | 1990.0000 in⁴ | 441.00 lbf/ft | 141.00 ft²/ft | 1910.00 in³ | 368.00 in³ | 130.00 in² | W36x441 | 194.0000 in⁴ | 661000.00 in⁶ | 0.950" | 1.360" | 17.000" |
| W36X487 | 0' - 7 1/2" | 8.550" | 19.650" | 1830.00 in³ | 263.00 in³ | 2.680" | 39.300" | 36000.0000 in⁴ | 2250.0000 in⁴ | 487.00 lbf/ft | 142.00 ft²/ft | 2130.00 in³ | 412.00 in³ | 143.00 in² | W36x487 | 258.0000 in⁴ | 754000.00 in⁶ | 0.950" | 1.500" | 17.100" |
| W36X529 | 0' - 7 1/2" | 8.600" | 19.900" | 1990.00 in³ | 289.00 in³ | 2.910" | 39.800" | 39600.0000 in⁴ | 2490.0000 in⁴ | 529.00 lbf/ft | 144.00 ft²/ft | 2330.00 in³ | 454.00 in³ | 156.00 in² | W36x529 | 327.0000 in⁴ | 846000.00 in⁶ | 0.950" | 1.610" | 17.200" |
| W36X652 | 0' - 7 1/2" | 8.800" | 20.550" | 2460.00 in³ | 367.00 in³ | 3.540" | 41.100" | 50600.0000 in⁴ | 3230.0000 in⁴ | 652.00 lbf/ft | 147.00 ft²/ft | 2910.00 in³ | 581.00 in³ | 192.00 in² | W36x652 | 593.0000 in⁴ | 1130000.00 in⁶ | 0.950" | 1.970" | 17.600" |
| W40X149 | 0' - 7 1/2" | 5.900" | 19.100" | 513.00 in³ | 38.80 in³ | 0.830" | 38.200" | 9800.0000 in⁴ | 229.0000 in⁴ | 149.00 lbf/ft | 120.00 ft²/ft | 598.00 in³ | 62.20 in³ | 43.80 in² | W40x149 | 9.3600 in⁴ | 80000.00 in⁶ | 1.180" | 0.630" | 11.800" |
| W40X167 | 0' - 7 1/2" | 5.900" | 19.300" | 600.00 in³ | 47.90 in³ | 1.030" | 38.600" | 11600.0000 in⁴ | 283.0000 in⁴ | 167.00 lbf/ft | 121.00 ft²/ft | 693.00 in³ | 76.00 in³ | 49.30 in² | W40x167 | 14.0000 in⁴ | 99700.00 in⁶ | 1.180" | 0.650" | 11.800" |
| W40X183 | 0' - 7 1/2" | 5.900" | 19.500" | 675.00 in³ | 56.00 in³ | 1.200" | 39.000" | 13200.0000 in⁴ | 331.0000 in⁴ | 183.00 lbf/ft | 122.00 ft²/ft | 774.00 in³ | 88.30 in³ | 53.30 in² | W40x183 | 19.3000 in⁴ | 118000.00 in⁶ | 1.180" | 0.650" | 11.800" |
| W40X199 | 0' - 7 1/2" | 7.900" | 19.350" | 770.00 in³ | 88.20 in³ | 1.070" | 38.700" | 14900.0000 in⁴ | 695.0000 in⁴ | 199.00 lbf/ft | 137.00 ft²/ft | 869.00 in³ | 137.00 in³ | 58.80 in² | W40x199 | 18.3000 in⁴ | 246000.00 in⁶ | 1.180" | 0.650" | 15.800" |
| W40X211 | 0' - 7 1/2" | 5.900" | 19.700" | 786.00 in³ | 66.10 in³ | 1.420" | 39.400" | 15500.0000 in⁴ | 390.0000 in⁴ | 211.00 lbf/ft | 122.00 ft²/ft | 906.00 in³ | 105.00 in³ | 62.10 in² | W40x211 | 30.4000 in⁴ | 141000.00 in⁶ | 1.180" | 0.750" | 11.800" |
| W40X215 | 0' - 7 1/2" | 7.900" | 19.500" | 859.00 in³ | 101.00 in³ | 1.220" | 39.000" | 16700.0000 in⁴ | 803.0000 in⁴ | 215.00 lbf/ft | 138.00 ft²/ft | 964.00 in³ | 156.00 in³ | 63.50 in² | W40x215 | 24.8000 in⁴ | 284000.00 in⁶ | 1.180" | 0.650" | 15.800" |
| W40X235 | 0' - 7 1/2" | 5.950" | 19.850" | 875.00 in³ | 74.60 in³ | 1.580" | 39.700" | 17400.0000 in⁴ | 444.0000 in⁴ | 235.00 lbf/ft | 123.00 ft²/ft | 1010.00 in³ | 118.00 in³ | 69.10 in² | W40x235 | 41.3000 in⁴ | 161000.00 in⁶ | 1.180" | 0.830" | 11.900" |
| W40X249 | 0' - 7 1/2" | 7.900" | 19.700" | 993.00 in³ | 118.00 in³ | 1.420" | 39.400" | 19600.0000 in⁴ | 926.0000 in⁴ | 249.00 lbf/ft | 138.00 ft²/ft | 1120.00 in³ | 182.00 in³ | 73.50 in² | W40x249 | 38.1000 in⁴ | 334000.00 in⁶ | 1.180" | 0.750" | 15.800" |
| W40X264 | 0' - 7 1/2" | 5.950" | 20.000" | 971.00 in³ | 82.60 in³ | 1.730" | 40.000" | 19400.0000 in⁴ | 493.0000 in⁴ | 264.00 lbf/ft | 124.00 ft²/ft | 1130.00 in³ | 132.00 in³ | 77.40 in² | W40x264 | 56.1000 in⁴ | 181000.00 in⁶ | 1.180" | 0.960" | 11.900" |
| W40X277 | 0' - 7 1/2" | 7.900" | 19.850" | 1100.00 in³ | 132.00 in³ | 1.580" | 39.700" | 21900.0000 in⁴ | 1040.0000 in⁴ | 277.00 lbf/ft | 139.00 ft²/ft | 1250.00 in³ | 204.00 in³ | 81.50 in² | W40x277 | 51.5000 in⁴ | 379000.00 in⁶ | 1.180" | 0.830" | 15.800" |
| W40X278 | 0' - 7 1/2" | 6.000" | 20.100" | 1020.00 in³ | 87.10 in³ | 1.810" | 40.200" | 20500.0000 in⁴ | 521.0000 in⁴ | 278.00 lbf/ft | 124.00 ft²/ft | 1190.00 in³ | 140.00 in³ | 82.30 in² | W40x278 | 65.0000 in⁴ | 192000.00 in⁶ | 1.180" | 1.030" | 12.000" |
| W40X294 | 0' - 7 1/2" | 6.000" | 20.200" | 1080.00 in³ | 93.50 in³ | 1.930" | 40.400" | 21900.0000 in⁴ | 562.0000 in⁴ | 294.00 lbf/ft | 125.00 ft²/ft | 1270.00 in³ | 150.00 in³ | 86.20 in² | W40x294 | 76.6000 in⁴ | 208000.00 in⁶ | 1.180" | 1.060" | 12.000" |
| W40X297 | 0' - 7 1/2" | 7.900" | 19.900" | 1170.00 in³ | 138.00 in³ | 1.650" | 39.800" | 23200.0000 in⁴ | 1090.0000 in⁴ | 297.00 lbf/ft | 139.00 ft²/ft | 1330.00 in³ | 215.00 in³ | 87.30 in² | W40x297 | 61.2000 in⁴ | 399000.00 in⁶ | 1.180" | 0.930" | 15.800" |
| W40X324 | 0' - 7 1/2" | 7.950" | 20.100" | 1280.00 in³ | 153.00 in³ | 1.810" | 40.200" | 25600.0000 in⁴ | 1220.0000 in⁴ | 324.00 lbf/ft | 140.00 ft²/ft | 1460.00 in³ | 239.00 in³ | 95.30 in² | W40x324 | 79.4000 in⁴ | 448000.00 in⁶ | 1.180" | 1.000" | 15.900" |
| W40X327 | 0' - 7 1/2" | 6.050" | 20.400" | 1200.00 in³ | 105.00 in³ | 2.130" | 40.800" | 24500.0000 in⁴ | 640.0000 in⁴ | 327.00 lbf/ft | 126.00 ft²/ft | 1410.00 in³ | 170.00 in³ | 95.90 in² | W40x327 | 103.0000 in⁴ | 239000.00 in⁶ | 1.180" | 1.180" | 12.100" |
| W40X331 | 0' - 7 1/2" | 6.100" | 20.400" | 1210.00 in³ | 106.00 in³ | 2.130" | 40.800" | 24700.0000 in⁴ | 644.0000 in⁴ | 331.00 lbf/ft | 126.00 ft²/ft | 1430.00 in³ | 172.00 in³ | 97.70 in² | W40x331 | 105.0000 in⁴ | 241000.00 in⁶ | 1.180" | 1.220" | 12.200" |
| W40X362 | 0' - 7 1/2" | 8.000" | 20.300" | 1420.00 in³ | 173.00 in³ | 2.010" | 40.600" | 28900.0000 in⁴ | 1380.0000 in⁴ | 362.00 lbf/ft | 141.00 ft²/ft | 1640.00 in³ | 270.00 in³ | 106.00 in² | W40x362 | 109.0000 in⁴ | 513000.00 in⁶ | 1.180" | 1.120" | 16.000" |
| W40X372 | 0' - 7 1/2" | 8.050" | 20.300" | 1460.00 in³ | 177.00 in³ | 2.050" | 40.600" | 29600.0000 in⁴ | 1420.0000 in⁴ | 372.00 lbf/ft | 141.00 ft²/ft | 1680.00 in³ | 277.00 in³ | 110.00 in² | W40x372 | 116.0000 in⁴ | 528000.00 in⁶ | 1.180" | 1.160" | 16.100" |
| W40X392 | 0' - 7 1/2" | 6.200" | 20.800" | 1440.00 in³ | 130.00 in³ | 2.520" | 41.600" | 29900.0000 in⁴ | 803.0000 in⁴ | 392.00 lbf/ft | 128.00 ft²/ft | 1710.00 in³ | 212.00 in³ | 116.00 in² | W40x392 | 172.0000 in⁴ | 306000.00 in⁶ | 1.180" | 1.420" | 12.400" |
| W40X397 | 0' - 7 1/2" | 8.050" | 20.500" | 1560.00 in³ | 191.00 in³ | 2.200" | 41.000" | 32000.0000 in⁴ | 1540.0000 in⁴ | 397.00 lbf/ft | 142.00 ft²/ft | 1800.00 in³ | 300.00 in³ | 117.00 in² | W40x397 | 142.0000 in⁴ | 579000.00 in⁶ | 1.180" | 1.220" | 16.100" |
| W40X431 | 0' - 7 1/2" | 8.100" | 20.650" | 1690.00 in³ | 208.00 in³ | 2.360" | 41.300" | 34800.0000 in⁴ | 1690.0000 in⁴ | 431.00 lbf/ft | 143.00 ft²/ft | 1960.00 in³ | 328.00 in³ | 127.00 in² | W40x431 | 177.0000 in⁴ | 638000.00 in⁶ | 1.180" | 1.340" | 16.200" |
| W40X503 | 0' - 7 1/2" | 8.200" | 21.050" | 1980.00 in³ | 249.00 in³ | 2.760" | 42.100" | 41600.0000 in⁴ | 2040.0000 in⁴ | 503.00 lbf/ft | 145.00 ft²/ft | 2320.00 in³ | 394.00 in³ | 148.00 in² | W40x503 | 277.0000 in⁴ | 789000.00 in⁶ | 1.180" | 1.540" | 16.400" |
| W40X593 | 0' - 7 1/2" | 8.350" | 21.500" | 2340.00 in³ | 302.00 in³ | 3.230" | 43.000" | 50400.0000 in⁴ | 2520.0000 in⁴ | 593.00 lbf/ft | 147.00 ft²/ft | 2760.00 in³ | 481.00 in³ | 174.00 in² | W40x593 | 445.0000 in⁴ | 997000.00 in⁶ | 1.180" | 1.790" | 16.700" |
| W44X230 | 0' - 5 1/2" | 7.900" | 21.450" | 971.00 in³ | 101.00 in³ | 1.220" | 42.900" | 20800.0000 in⁴ | 796.0000 in⁴ | 230.00 lbf/ft | 146.00 ft²/ft | 1100.00 in³ | 157.00 in³ | 67.80 in² | W44x230 | 24.9000 in⁴ | 346000.00 in⁶ | 0.790" | 0.710" | 15.800" |
| W44X262 | 0' - 5 1/2" | 7.900" | 21.650" | 1110.00 in³ | 117.00 in³ | 1.420" | 43.300" | 24100.0000 in⁴ | 923.0000 in⁴ | 262.00 lbf/ft | 147.00 ft²/ft | 1270.00 in³ | 182.00 in³ | 77.20 in² | W44x262 | 37.3000 in⁴ | 405000.00 in⁶ | 0.780" | 0.785" | 15.800" |
| W44X290 | 0' - 5 1/2" | 7.900" | 21.800" | 1240.00 in³ | 132.00 in³ | 1.580" | 43.600" | 27000.0000 in⁴ | 1040.0000 in⁴ | 290.00 lbf/ft | 147.00 ft²/ft | 1410.00 in³ | 205.00 in³ | 85.40 in² | W44x290 | 50.9000 in⁴ | 461000.00 in⁶ | 0.780" | 0.865" | 15.800" |
| W44X335 | 0' - 5 1/2" | 7.950" | 22.000" | 1410.00 in³ | 150.00 in³ | 1.770" | 44.000" | 31100.0000 in⁴ | 1200.0000 in⁴ | 335.00 lbf/ft | 148.00 ft²/ft | 1620.00 in³ | 236.00 in³ | 98.50 in² | W44x335 | 74.7000 in⁴ | 535000.00 in⁶ | 0.790" | 1.030" | 15.900" |

## geometry (parser evidence)
native form markers: Sweep x2
no freeform markers — native parametric forms only
